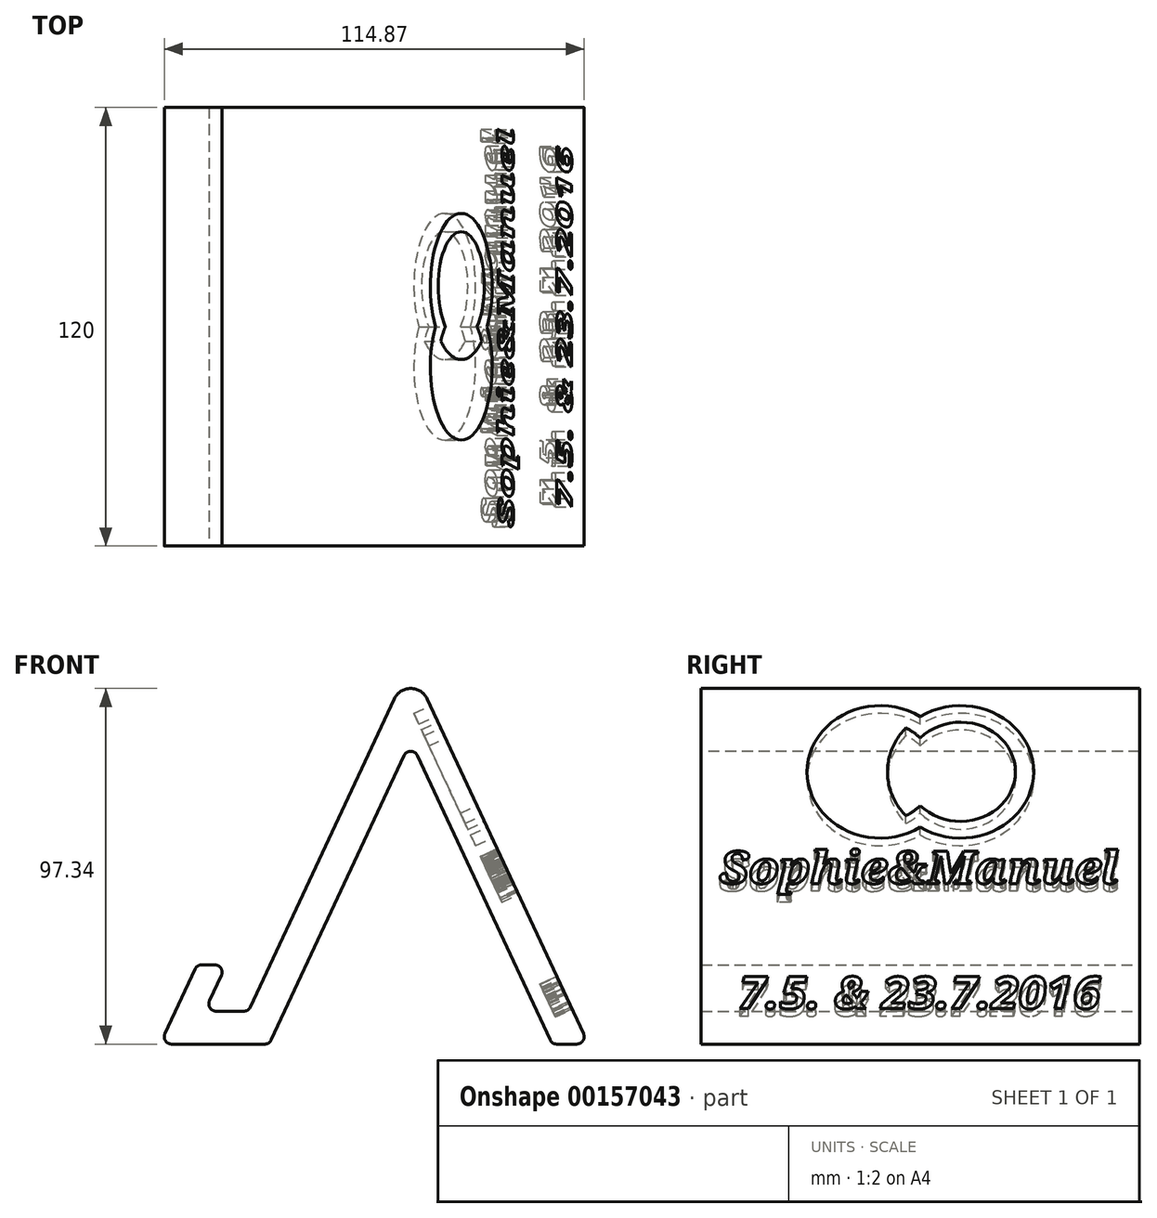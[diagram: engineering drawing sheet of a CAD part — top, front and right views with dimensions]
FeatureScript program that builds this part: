
annotation { "Feature Type Name" : "Feature", "Feature Type Description" : "" }
export const myFeature = defineFeature(function(context is Context, id is Id, definition is map)
    precondition{}
    {
        {
            var Q0;
            Q0=qCreatedBy(makeId("Front.planeOp"),FACE);
            var sketch = newSketch(context, id + "F0", { "sketchPlane" : qUnion([Q0])});
            skLineSegment(sketch, "E0", {"start": v(-35.91, 1.37) * mm, "end": v(-27.91, 1.37) * mm});
            skLineSegment(sketch, "E1", {"start": v(-27.91, 1.37) * mm, "end": v(-33.83, -11.32) * mm});
            skLineSegment(sketch, "E2", {"start": v(-33.83, -11.32) * mm, "end": v(-21.83, -11.32) * mm});
            skLineSegment(sketch, "E3", {"start": v(-21.83, -11.32) * mm, "end": v(22.55, 83.85) * mm});
            skLineSegment(sketch, "E4", {"start": v(22.55, 83.85) * mm, "end": v(22.55, 83.85) * mm});
            skLineSegment(sketch, "E5", {"start": v(22.55, 83.85) * mm, "end": v(71.12, -20.32) * mm});
            skLineSegment(sketch, "E6", {"start": v(71.12, -20.32) * mm, "end": v(61.19, -20.32) * mm});
            skLineSegment(sketch, "E7", {"start": v(61.19, -20.32) * mm, "end": v(22.55, 62.55) * mm});
            skLineSegment(sketch, "E8", {"start": v(22.55, 62.55) * mm, "end": v(-16.1, -20.32) * mm});
            skLineSegment(sketch, "E9", {"start": v(-46.03, -20.32) * mm, "end": v(-35.91, 1.37) * mm});
            skLineSegment(sketch, "E10", {"start": v(-16.1, -20.32) * mm, "end": v(61.19, -20.32) * mm, "construction": true});
            skLineSegment(sketch, "E11", {"start": v(-46.03, -20.32) * mm, "end": v(-16.1, -20.32) * mm});
            skSolve(sketch);
        }
        {
            var Q0;
            Q0=makeQuery(id+"F0.imprint","IMPRINT",FACE,{"disambiguationData":[TD([[makeQuery(id+"F0.imprint","IMPRINT",EDGE,{"derivedFrom":sQuery(id+"F0.wireOp",EDGE,"E0")}),-1.0]])]});
            extrude(context, id + "F1", {"entities" : qUnion([Q0]), "depth" : 120 * mm});
        }
        {
            var Q0;
            Q0=makeQuery(id+"F1.opExtrude","SWEPT_FACE",FACE,{"disambiguationData":[OSD([sQuery(id+"F0.wireOp",EDGE,"E5")])]});
            var sketch = newSketch(context, id + "F2", { "sketchPlane" : qUnion([Q0])});
            skText(sketch, "E12", { "text": "Sophie&Manuel", "fontName": "NotoSerif-BoldItalic.ttf"});
            skLineSegment(sketch, "E13", {"start": v(-120, 23.74) * mm, "end": v(0, 23.74) * mm, "construction": true});
            skLineSegment(sketch, "E14", {"start": v(-60, 23.74) * mm, "end": v(-60, 33.74) * mm, "construction": true});
            skLineSegment(sketch, "E15", {"start": v(-60, 33.74) * mm, "end": v(-71, 33.74) * mm, "construction": true});
            skLineSegment(sketch, "E16", {"start": v(-60, 33.74) * mm, "end": v(-49, 33.74) * mm, "construction": true});
            skCircle(sketch, "E17", {"center": v(-71, 33.74) * mm, "radius": 20 * mm});
            skCircle(sketch, "E18", {"center": v(-71, 33.74) * mm, "radius": 15 * mm});
            skCircle(sketch, "E19", {"center": v(-49, 33.74) * mm, "radius": 15 * mm});
            skCircle(sketch, "E20", {"center": v(-49, 33.74) * mm, "radius": 20 * mm});
            skLineSegment(sketch, "E21", {"start": v(-60, 0) * mm, "end": v(-60, -48.47) * mm, "construction": true});
            skText(sketch, "E22", { "text": "7.5. & 23.7.2016", "fontName": "OpenSans-BoldItalic.ttf"});
            const initialGuessF2  = {"E12": [-0.115, 0, 1, 0, 0.00981], "E22": [-0.10981, -0.03778, 1, 0, 0.00973]};
            skSetInitialGuess(sketch, initialGuessF2);
            skSolve(sketch);
        }
        {
            var Q0;
            Q0=makeQuery(id+"F2.imprint","IMPRINT",FACE,{"disambiguationData":[TD([[makeQuery(id+"F2.imprint","IMPRINT",EDGE,{"derivedFrom":sQuery(id+"F2.wireOp",EDGE,"E12.sketch_text.stroke-154")}),-1.0]])]});
            var Q1;
            Q1=makeQuery(id+"F2.imprint","IMPRINT",FACE,{"disambiguationData":[TD([[makeQuery(id+"F2.imprint","IMPRINT",EDGE,{"derivedFrom":sQuery(id+"F2.wireOp",EDGE,"E12.sketch_text.stroke-88")}),-1.0]])]});
            var Q2;
            Q2=makeQuery(id+"F2.imprint","IMPRINT",FACE,{"disambiguationData":[TD([[makeQuery(id+"F2.imprint","IMPRINT",EDGE,{"derivedFrom":sQuery(id+"F2.wireOp",EDGE,"E12.sketch_text.stroke-52")}),-1.0]])]});
            var Q3;
            Q3 = qSketchRegion(id + "F2", true);
            var Q4;
            {var subQ0=sQuery(id+"F2.wireOp",EDGE,"E19");var subQ1=sQuery(id+"F2.wireOp",EDGE,"E17");var subQ2=makeQuery(id+"F2.imprint","INTERSECT",VERTEX,{"disambiguationData":[OD(0.0)],"derivedFrom":[subQ1,subQ0]});Q4=makeQuery(id+"F2.imprint","IMPRINT",FACE,{"disambiguationData":[TD([[makeQuery(id+"F2.imprint","IMPRINT",EDGE,{"disambiguationData":[TD([[subQ2,1.0]])],"derivedFrom":subQ1}),1.0]])]});}
            var Q5;
            {var subQ0=sQuery(id+"F2.wireOp",EDGE,"E20");var subQ1=sQuery(id+"F2.wireOp",EDGE,"E18");var subQ2=makeQuery(id+"F2.imprint","INTERSECT",VERTEX,{"disambiguationData":[OD(0.0)],"derivedFrom":[subQ1,subQ0]});Q5=makeQuery(id+"F2.imprint","IMPRINT",FACE,{"disambiguationData":[TD([[makeQuery(id+"F2.imprint","IMPRINT",EDGE,{"disambiguationData":[TD([[subQ2,1.0]])],"derivedFrom":subQ1}),1.0]])]});}
            extrude(context, id + "F3", {"entities" : qUnion([Q0, Q1, Q2, Q3, Q4, Q5]), "operationType" : NewBodyOperationType.REMOVE, "oppositeDirection" : true, "depth" : 5 * mm});
        }
        {
            var Q0;
            Q0=makeQuery(id+"F1.opExtrude","SWEPT_EDGE",EDGE,{"disambiguationData":[OSD([sQuery(id+"F0.wireOp",EDGE,"E3"),sQuery(id+"F0.wireOp",EDGE,"E5")])]});
            fillet(context, id + "F4", {"entities" : qUnion([Q0]), "radius" : 5 * mm, "tangentPropagation" : true, "allowEdgeOverflow" : false});
        }
        {
            var Q0;
            Q0=makeQuery(id+"F1.opExtrude","SWEPT_EDGE",EDGE,{"disambiguationData":[OSD([sQuery(id+"F0.wireOp",EDGE,"E0"),sQuery(id+"F0.wireOp",EDGE,"E1")])]});
            var Q1;
            Q1=makeQuery(id+"F1.opExtrude","SWEPT_EDGE",EDGE,{"disambiguationData":[OSD([sQuery(id+"F0.wireOp",EDGE,"E0"),sQuery(id+"F0.wireOp",EDGE,"E9")])]});
            var Q2;
            Q2=makeQuery(id+"F1.opExtrude","SWEPT_EDGE",EDGE,{"disambiguationData":[OSD([sQuery(id+"F0.wireOp",EDGE,"E1"),sQuery(id+"F0.wireOp",EDGE,"E2")])]});
            var Q3;
            Q3=makeQuery(id+"F1.opExtrude","SWEPT_EDGE",EDGE,{"disambiguationData":[OSD([sQuery(id+"F0.wireOp",EDGE,"E2"),sQuery(id+"F0.wireOp",EDGE,"E3")])]});
            var Q4;
            Q4=makeQuery(id+"F1.opExtrude","SWEPT_EDGE",EDGE,{"disambiguationData":[OSD([sQuery(id+"F0.wireOp",EDGE,"E9"),sQuery(id+"F0.wireOp",EDGE,"E11")])]});
            var Q5;
            Q5=makeQuery(id+"F1.opExtrude","SWEPT_EDGE",EDGE,{"disambiguationData":[OSD([sQuery(id+"F0.wireOp",EDGE,"E8"),sQuery(id+"F0.wireOp",EDGE,"E11")])]});
            var Q6;
            Q6=makeQuery(id+"F1.opExtrude","SWEPT_EDGE",EDGE,{"disambiguationData":[OSD([sQuery(id+"F0.wireOp",EDGE,"E6"),sQuery(id+"F0.wireOp",EDGE,"E7")])]});
            var Q7;
            Q7=makeQuery(id+"F1.opExtrude","SWEPT_EDGE",EDGE,{"disambiguationData":[OSD([sQuery(id+"F0.wireOp",EDGE,"E5"),sQuery(id+"F0.wireOp",EDGE,"E6")])]});
            fillet(context, id + "F5", {"entities" : qUnion([Q0, Q1, Q2, Q3, Q4, Q5, Q6, Q7]), "radius" : 2 * mm, "tangentPropagation" : true, "allowEdgeOverflow" : false});
        }
        {
            var Q0;
            Q0=makeQuery(id+"F1.opExtrude","SWEPT_EDGE",EDGE,{"disambiguationData":[OSD([sQuery(id+"F0.wireOp",EDGE,"E7"),sQuery(id+"F0.wireOp",EDGE,"E8")])]});
            fillet(context, id + "F6", {"entities" : qUnion([Q0]), "radius" : 2 * mm, "tangentPropagation" : true, "allowEdgeOverflow" : false});
        }
        {
            var Q0;
            Q0=makeQuery(id+"F3.boolean.opBoolean","COPY",FACE,{"derivedFrom":makeQuery(id+"F3.opExtrude","CAP_FACE",FACE,{"disambiguationData":[OSD([sQuery(id+"F2.wireOp",EDGE,"E12.sketch_text.stroke-52"),sQuery(id+"F2.wireOp",EDGE,"E12.sketch_text.stroke-53"),sQuery(id+"F2.wireOp",EDGE,"E12.sketch_text.stroke-54"),sQuery(id+"F2.wireOp",EDGE,"E12.sketch_text.stroke-55"),sQuery(id+"F2.wireOp",EDGE,"E12.sketch_text.stroke-56"),sQuery(id+"F2.wireOp",EDGE,"E12.sketch_text.stroke-57"),sQuery(id+"F2.wireOp",EDGE,"E12.sketch_text.stroke-58"),sQuery(id+"F2.wireOp",EDGE,"E12.sketch_text.stroke-59"),sQuery(id+"F2.wireOp",EDGE,"E12.sketch_text.stroke-60"),sQuery(id+"F2.wireOp",EDGE,"E12.sketch_text.stroke-61"),sQuery(id+"F2.wireOp",EDGE,"E12.sketch_text.stroke-62"),sQuery(id+"F2.wireOp",EDGE,"E12.sketch_text.stroke-63"),sQuery(id+"F2.wireOp",EDGE,"E12.sketch_text.stroke-64"),sQuery(id+"F2.wireOp",EDGE,"E12.sketch_text.stroke-65"),sQuery(id+"F2.wireOp",EDGE,"E12.sketch_text.stroke-66"),sQuery(id+"F2.wireOp",EDGE,"E12.sketch_text.stroke-67"),sQuery(id+"F2.wireOp",EDGE,"E12.sketch_text.stroke-68"),sQuery(id+"F2.wireOp",EDGE,"E12.sketch_text.stroke-69"),sQuery(id+"F2.wireOp",EDGE,"E12.sketch_text.stroke-70"),sQuery(id+"F2.wireOp",EDGE,"E12.sketch_text.stroke-71"),sQuery(id+"F2.wireOp",EDGE,"E12.sketch_text.stroke-72"),sQuery(id+"F2.wireOp",EDGE,"E12.sketch_text.stroke-73"),sQuery(id+"F2.wireOp",EDGE,"E12.sketch_text.stroke-74"),sQuery(id+"F2.wireOp",EDGE,"E12.sketch_text.stroke-75"),sQuery(id+"F2.wireOp",EDGE,"E12.sketch_text.stroke-76"),sQuery(id+"F2.wireOp",EDGE,"E12.sketch_text.stroke-77"),sQuery(id+"F2.wireOp",EDGE,"E12.sketch_text.stroke-78"),sQuery(id+"F2.wireOp",EDGE,"E12.sketch_text.stroke-79"),sQuery(id+"F2.wireOp",EDGE,"E12.sketch_text.stroke-80"),sQuery(id+"F2.wireOp",EDGE,"E12.sketch_text.stroke-81"),sQuery(id+"F2.wireOp",EDGE,"E12.sketch_text.stroke-82"),sQuery(id+"F2.wireOp",EDGE,"E12.sketch_text.stroke-83"),sQuery(id+"F2.wireOp",EDGE,"E12.sketch_text.stroke-84"),sQuery(id+"F2.wireOp",EDGE,"E12.sketch_text.stroke-85"),sQuery(id+"F2.wireOp",EDGE,"E12.sketch_text.stroke-86"),sQuery(id+"F2.wireOp",EDGE,"E12.sketch_text.stroke-87")])],"isStart":false})});
            var Q1;
            Q1=makeQuery(id+"F3.boolean.opBoolean","COPY",FACE,{"derivedFrom":makeQuery(id+"F3.opExtrude","CAP_FACE",FACE,{"disambiguationData":[OSD([sQuery(id+"F2.wireOp",EDGE,"E12.sketch_text.stroke-0"),sQuery(id+"F2.wireOp",EDGE,"E12.sketch_text.stroke-1"),sQuery(id+"F2.wireOp",EDGE,"E12.sketch_text.stroke-2"),sQuery(id+"F2.wireOp",EDGE,"E12.sketch_text.stroke-3"),sQuery(id+"F2.wireOp",EDGE,"E12.sketch_text.stroke-4"),sQuery(id+"F2.wireOp",EDGE,"E12.sketch_text.stroke-5"),sQuery(id+"F2.wireOp",EDGE,"E12.sketch_text.stroke-6"),sQuery(id+"F2.wireOp",EDGE,"E12.sketch_text.stroke-7"),sQuery(id+"F2.wireOp",EDGE,"E12.sketch_text.stroke-8"),sQuery(id+"F2.wireOp",EDGE,"E12.sketch_text.stroke-9"),sQuery(id+"F2.wireOp",EDGE,"E12.sketch_text.stroke-10"),sQuery(id+"F2.wireOp",EDGE,"E12.sketch_text.stroke-11"),sQuery(id+"F2.wireOp",EDGE,"E12.sketch_text.stroke-12"),sQuery(id+"F2.wireOp",EDGE,"E12.sketch_text.stroke-13"),sQuery(id+"F2.wireOp",EDGE,"E12.sketch_text.stroke-14"),sQuery(id+"F2.wireOp",EDGE,"E12.sketch_text.stroke-15"),sQuery(id+"F2.wireOp",EDGE,"E12.sketch_text.stroke-16"),sQuery(id+"F2.wireOp",EDGE,"E12.sketch_text.stroke-17"),sQuery(id+"F2.wireOp",EDGE,"E12.sketch_text.stroke-18"),sQuery(id+"F2.wireOp",EDGE,"E12.sketch_text.stroke-19"),sQuery(id+"F2.wireOp",EDGE,"E12.sketch_text.stroke-20"),sQuery(id+"F2.wireOp",EDGE,"E12.sketch_text.stroke-21"),sQuery(id+"F2.wireOp",EDGE,"E12.sketch_text.stroke-22"),sQuery(id+"F2.wireOp",EDGE,"E12.sketch_text.stroke-23"),sQuery(id+"F2.wireOp",EDGE,"E12.sketch_text.stroke-24"),sQuery(id+"F2.wireOp",EDGE,"E12.sketch_text.stroke-25"),sQuery(id+"F2.wireOp",EDGE,"E12.sketch_text.stroke-26"),sQuery(id+"F2.wireOp",EDGE,"E12.sketch_text.stroke-27"),sQuery(id+"F2.wireOp",EDGE,"E12.sketch_text.stroke-28"),sQuery(id+"F2.wireOp",EDGE,"E12.sketch_text.stroke-29"),sQuery(id+"F2.wireOp",EDGE,"E12.sketch_text.stroke-30"),sQuery(id+"F2.wireOp",EDGE,"E12.sketch_text.stroke-31"),sQuery(id+"F2.wireOp",EDGE,"E12.sketch_text.stroke-32"),sQuery(id+"F2.wireOp",EDGE,"E12.sketch_text.stroke-33"),sQuery(id+"F2.wireOp",EDGE,"E12.sketch_text.stroke-34"),sQuery(id+"F2.wireOp",EDGE,"E12.sketch_text.stroke-35"),sQuery(id+"F2.wireOp",EDGE,"E12.sketch_text.stroke-36"),sQuery(id+"F2.wireOp",EDGE,"E12.sketch_text.stroke-37"),sQuery(id+"F2.wireOp",EDGE,"E12.sketch_text.stroke-38"),sQuery(id+"F2.wireOp",EDGE,"E12.sketch_text.stroke-39"),sQuery(id+"F2.wireOp",EDGE,"E12.sketch_text.stroke-40"),sQuery(id+"F2.wireOp",EDGE,"E12.sketch_text.stroke-41"),sQuery(id+"F2.wireOp",EDGE,"E12.sketch_text.stroke-42"),sQuery(id+"F2.wireOp",EDGE,"E12.sketch_text.stroke-43"),sQuery(id+"F2.wireOp",EDGE,"E12.sketch_text.stroke-44"),sQuery(id+"F2.wireOp",EDGE,"E12.sketch_text.stroke-45"),sQuery(id+"F2.wireOp",EDGE,"E12.sketch_text.stroke-46"),sQuery(id+"F2.wireOp",EDGE,"E12.sketch_text.stroke-47"),sQuery(id+"F2.wireOp",EDGE,"E12.sketch_text.stroke-48"),sQuery(id+"F2.wireOp",EDGE,"E12.sketch_text.stroke-49"),sQuery(id+"F2.wireOp",EDGE,"E12.sketch_text.stroke-50"),sQuery(id+"F2.wireOp",EDGE,"E12.sketch_text.stroke-51")])],"isStart":false})});
            var Q2;
            Q2=makeQuery(id+"F3.boolean.opBoolean","COPY",FACE,{"derivedFrom":makeQuery(id+"F3.opExtrude","CAP_FACE",FACE,{"disambiguationData":[OSD([sQuery(id+"F2.wireOp",EDGE,"E12.sketch_text.stroke-88"),sQuery(id+"F2.wireOp",EDGE,"E12.sketch_text.stroke-89"),sQuery(id+"F2.wireOp",EDGE,"E12.sketch_text.stroke-90"),sQuery(id+"F2.wireOp",EDGE,"E12.sketch_text.stroke-91"),sQuery(id+"F2.wireOp",EDGE,"E12.sketch_text.stroke-92"),sQuery(id+"F2.wireOp",EDGE,"E12.sketch_text.stroke-93"),sQuery(id+"F2.wireOp",EDGE,"E12.sketch_text.stroke-94"),sQuery(id+"F2.wireOp",EDGE,"E12.sketch_text.stroke-95"),sQuery(id+"F2.wireOp",EDGE,"E12.sketch_text.stroke-96"),sQuery(id+"F2.wireOp",EDGE,"E12.sketch_text.stroke-97"),sQuery(id+"F2.wireOp",EDGE,"E12.sketch_text.stroke-98"),sQuery(id+"F2.wireOp",EDGE,"E12.sketch_text.stroke-99"),sQuery(id+"F2.wireOp",EDGE,"E12.sketch_text.stroke-100"),sQuery(id+"F2.wireOp",EDGE,"E12.sketch_text.stroke-101"),sQuery(id+"F2.wireOp",EDGE,"E12.sketch_text.stroke-102"),sQuery(id+"F2.wireOp",EDGE,"E12.sketch_text.stroke-103"),sQuery(id+"F2.wireOp",EDGE,"E12.sketch_text.stroke-104"),sQuery(id+"F2.wireOp",EDGE,"E12.sketch_text.stroke-105"),sQuery(id+"F2.wireOp",EDGE,"E12.sketch_text.stroke-106"),sQuery(id+"F2.wireOp",EDGE,"E12.sketch_text.stroke-107"),sQuery(id+"F2.wireOp",EDGE,"E12.sketch_text.stroke-108"),sQuery(id+"F2.wireOp",EDGE,"E12.sketch_text.stroke-109"),sQuery(id+"F2.wireOp",EDGE,"E12.sketch_text.stroke-110"),sQuery(id+"F2.wireOp",EDGE,"E12.sketch_text.stroke-111"),sQuery(id+"F2.wireOp",EDGE,"E12.sketch_text.stroke-112"),sQuery(id+"F2.wireOp",EDGE,"E12.sketch_text.stroke-113"),sQuery(id+"F2.wireOp",EDGE,"E12.sketch_text.stroke-114"),sQuery(id+"F2.wireOp",EDGE,"E12.sketch_text.stroke-115"),sQuery(id+"F2.wireOp",EDGE,"E12.sketch_text.stroke-116"),sQuery(id+"F2.wireOp",EDGE,"E12.sketch_text.stroke-117"),sQuery(id+"F2.wireOp",EDGE,"E12.sketch_text.stroke-118"),sQuery(id+"F2.wireOp",EDGE,"E12.sketch_text.stroke-119"),sQuery(id+"F2.wireOp",EDGE,"E12.sketch_text.stroke-120"),sQuery(id+"F2.wireOp",EDGE,"E12.sketch_text.stroke-121"),sQuery(id+"F2.wireOp",EDGE,"E12.sketch_text.stroke-122"),sQuery(id+"F2.wireOp",EDGE,"E12.sketch_text.stroke-123"),sQuery(id+"F2.wireOp",EDGE,"E12.sketch_text.stroke-124"),sQuery(id+"F2.wireOp",EDGE,"E12.sketch_text.stroke-125"),sQuery(id+"F2.wireOp",EDGE,"E12.sketch_text.stroke-126"),sQuery(id+"F2.wireOp",EDGE,"E12.sketch_text.stroke-127"),sQuery(id+"F2.wireOp",EDGE,"E12.sketch_text.stroke-128"),sQuery(id+"F2.wireOp",EDGE,"E12.sketch_text.stroke-129"),sQuery(id+"F2.wireOp",EDGE,"E12.sketch_text.stroke-130"),sQuery(id+"F2.wireOp",EDGE,"E12.sketch_text.stroke-131"),sQuery(id+"F2.wireOp",EDGE,"E12.sketch_text.stroke-132"),sQuery(id+"F2.wireOp",EDGE,"E12.sketch_text.stroke-133"),sQuery(id+"F2.wireOp",EDGE,"E12.sketch_text.stroke-134"),sQuery(id+"F2.wireOp",EDGE,"E12.sketch_text.stroke-135"),sQuery(id+"F2.wireOp",EDGE,"E12.sketch_text.stroke-136"),sQuery(id+"F2.wireOp",EDGE,"E12.sketch_text.stroke-137"),sQuery(id+"F2.wireOp",EDGE,"E12.sketch_text.stroke-138"),sQuery(id+"F2.wireOp",EDGE,"E12.sketch_text.stroke-139"),sQuery(id+"F2.wireOp",EDGE,"E12.sketch_text.stroke-140"),sQuery(id+"F2.wireOp",EDGE,"E12.sketch_text.stroke-141"),sQuery(id+"F2.wireOp",EDGE,"E12.sketch_text.stroke-142"),sQuery(id+"F2.wireOp",EDGE,"E12.sketch_text.stroke-143"),sQuery(id+"F2.wireOp",EDGE,"E12.sketch_text.stroke-144"),sQuery(id+"F2.wireOp",EDGE,"E12.sketch_text.stroke-145"),sQuery(id+"F2.wireOp",EDGE,"E12.sketch_text.stroke-146"),sQuery(id+"F2.wireOp",EDGE,"E12.sketch_text.stroke-147"),sQuery(id+"F2.wireOp",EDGE,"E12.sketch_text.stroke-148"),sQuery(id+"F2.wireOp",EDGE,"E12.sketch_text.stroke-149"),sQuery(id+"F2.wireOp",EDGE,"E12.sketch_text.stroke-150"),sQuery(id+"F2.wireOp",EDGE,"E12.sketch_text.stroke-151"),sQuery(id+"F2.wireOp",EDGE,"E12.sketch_text.stroke-152"),sQuery(id+"F2.wireOp",EDGE,"E12.sketch_text.stroke-153")])],"isStart":false})});
            var Q3;
            Q3=makeQuery(id+"F3.boolean.opBoolean","COPY",FACE,{"derivedFrom":makeQuery(id+"F3.opExtrude","CAP_FACE",FACE,{"disambiguationData":[OSD([sQuery(id+"F2.wireOp",EDGE,"E12.sketch_text.stroke-154"),sQuery(id+"F2.wireOp",EDGE,"E12.sketch_text.stroke-155"),sQuery(id+"F2.wireOp",EDGE,"E12.sketch_text.stroke-156"),sQuery(id+"F2.wireOp",EDGE,"E12.sketch_text.stroke-157"),sQuery(id+"F2.wireOp",EDGE,"E12.sketch_text.stroke-158"),sQuery(id+"F2.wireOp",EDGE,"E12.sketch_text.stroke-159"),sQuery(id+"F2.wireOp",EDGE,"E12.sketch_text.stroke-160"),sQuery(id+"F2.wireOp",EDGE,"E12.sketch_text.stroke-161"),sQuery(id+"F2.wireOp",EDGE,"E12.sketch_text.stroke-162"),sQuery(id+"F2.wireOp",EDGE,"E12.sketch_text.stroke-163"),sQuery(id+"F2.wireOp",EDGE,"E12.sketch_text.stroke-164"),sQuery(id+"F2.wireOp",EDGE,"E12.sketch_text.stroke-165"),sQuery(id+"F2.wireOp",EDGE,"E12.sketch_text.stroke-166"),sQuery(id+"F2.wireOp",EDGE,"E12.sketch_text.stroke-167"),sQuery(id+"F2.wireOp",EDGE,"E12.sketch_text.stroke-168"),sQuery(id+"F2.wireOp",EDGE,"E12.sketch_text.stroke-169"),sQuery(id+"F2.wireOp",EDGE,"E12.sketch_text.stroke-170"),sQuery(id+"F2.wireOp",EDGE,"E12.sketch_text.stroke-171"),sQuery(id+"F2.wireOp",EDGE,"E12.sketch_text.stroke-172"),sQuery(id+"F2.wireOp",EDGE,"E12.sketch_text.stroke-173"),sQuery(id+"F2.wireOp",EDGE,"E12.sketch_text.stroke-174"),sQuery(id+"F2.wireOp",EDGE,"E12.sketch_text.stroke-175"),sQuery(id+"F2.wireOp",EDGE,"E12.sketch_text.stroke-176"),sQuery(id+"F2.wireOp",EDGE,"E12.sketch_text.stroke-177"),sQuery(id+"F2.wireOp",EDGE,"E12.sketch_text.stroke-178"),sQuery(id+"F2.wireOp",EDGE,"E12.sketch_text.stroke-179"),sQuery(id+"F2.wireOp",EDGE,"E12.sketch_text.stroke-180"),sQuery(id+"F2.wireOp",EDGE,"E12.sketch_text.stroke-181"),sQuery(id+"F2.wireOp",EDGE,"E12.sketch_text.stroke-182"),sQuery(id+"F2.wireOp",EDGE,"E12.sketch_text.stroke-183"),sQuery(id+"F2.wireOp",EDGE,"E12.sketch_text.stroke-184"),sQuery(id+"F2.wireOp",EDGE,"E12.sketch_text.stroke-185"),sQuery(id+"F2.wireOp",EDGE,"E12.sketch_text.stroke-186"),sQuery(id+"F2.wireOp",EDGE,"E12.sketch_text.stroke-187"),sQuery(id+"F2.wireOp",EDGE,"E12.sketch_text.stroke-188"),sQuery(id+"F2.wireOp",EDGE,"E12.sketch_text.stroke-189"),sQuery(id+"F2.wireOp",EDGE,"E12.sketch_text.stroke-190"),sQuery(id+"F2.wireOp",EDGE,"E12.sketch_text.stroke-191"),sQuery(id+"F2.wireOp",EDGE,"E12.sketch_text.stroke-192"),sQuery(id+"F2.wireOp",EDGE,"E12.sketch_text.stroke-193"),sQuery(id+"F2.wireOp",EDGE,"E12.sketch_text.stroke-194"),sQuery(id+"F2.wireOp",EDGE,"E12.sketch_text.stroke-195"),sQuery(id+"F2.wireOp",EDGE,"E12.sketch_text.stroke-196"),sQuery(id+"F2.wireOp",EDGE,"E12.sketch_text.stroke-197"),sQuery(id+"F2.wireOp",EDGE,"E12.sketch_text.stroke-198"),sQuery(id+"F2.wireOp",EDGE,"E12.sketch_text.stroke-199"),sQuery(id+"F2.wireOp",EDGE,"E12.sketch_text.stroke-200"),sQuery(id+"F2.wireOp",EDGE,"E12.sketch_text.stroke-201"),sQuery(id+"F2.wireOp",EDGE,"E12.sketch_text.stroke-202"),sQuery(id+"F2.wireOp",EDGE,"E12.sketch_text.stroke-203"),sQuery(id+"F2.wireOp",EDGE,"E12.sketch_text.stroke-204"),sQuery(id+"F2.wireOp",EDGE,"E12.sketch_text.stroke-205"),sQuery(id+"F2.wireOp",EDGE,"E12.sketch_text.stroke-206"),sQuery(id+"F2.wireOp",EDGE,"E12.sketch_text.stroke-207"),sQuery(id+"F2.wireOp",EDGE,"E12.sketch_text.stroke-208"),sQuery(id+"F2.wireOp",EDGE,"E12.sketch_text.stroke-209"),sQuery(id+"F2.wireOp",EDGE,"E12.sketch_text.stroke-210"),sQuery(id+"F2.wireOp",EDGE,"E12.sketch_text.stroke-211"),sQuery(id+"F2.wireOp",EDGE,"E12.sketch_text.stroke-212"),sQuery(id+"F2.wireOp",EDGE,"E12.sketch_text.stroke-213"),sQuery(id+"F2.wireOp",EDGE,"E12.sketch_text.stroke-214"),sQuery(id+"F2.wireOp",EDGE,"E12.sketch_text.stroke-215")])],"isStart":false})});
            var Q4;
            Q4=makeQuery(id+"F3.boolean.opBoolean","COPY",FACE,{"derivedFrom":makeQuery(id+"F3.opExtrude","CAP_FACE",FACE,{"disambiguationData":[OSD([sQuery(id+"F2.wireOp",EDGE,"E12.sketch_text.stroke-216"),sQuery(id+"F2.wireOp",EDGE,"E12.sketch_text.stroke-217"),sQuery(id+"F2.wireOp",EDGE,"E12.sketch_text.stroke-218"),sQuery(id+"F2.wireOp",EDGE,"E12.sketch_text.stroke-219"),sQuery(id+"F2.wireOp",EDGE,"E12.sketch_text.stroke-220"),sQuery(id+"F2.wireOp",EDGE,"E12.sketch_text.stroke-221"),sQuery(id+"F2.wireOp",EDGE,"E12.sketch_text.stroke-222"),sQuery(id+"F2.wireOp",EDGE,"E12.sketch_text.stroke-223"),sQuery(id+"F2.wireOp",EDGE,"E12.sketch_text.stroke-224"),sQuery(id+"F2.wireOp",EDGE,"E12.sketch_text.stroke-225"),sQuery(id+"F2.wireOp",EDGE,"E12.sketch_text.stroke-226"),sQuery(id+"F2.wireOp",EDGE,"E12.sketch_text.stroke-227"),sQuery(id+"F2.wireOp",EDGE,"E12.sketch_text.stroke-228"),sQuery(id+"F2.wireOp",EDGE,"E12.sketch_text.stroke-229"),sQuery(id+"F2.wireOp",EDGE,"E12.sketch_text.stroke-230"),sQuery(id+"F2.wireOp",EDGE,"E12.sketch_text.stroke-231"),sQuery(id+"F2.wireOp",EDGE,"E12.sketch_text.stroke-232"),sQuery(id+"F2.wireOp",EDGE,"E12.sketch_text.stroke-233"),sQuery(id+"F2.wireOp",EDGE,"E12.sketch_text.stroke-234"),sQuery(id+"F2.wireOp",EDGE,"E12.sketch_text.stroke-235"),sQuery(id+"F2.wireOp",EDGE,"E12.sketch_text.stroke-236"),sQuery(id+"F2.wireOp",EDGE,"E12.sketch_text.stroke-237"),sQuery(id+"F2.wireOp",EDGE,"E12.sketch_text.stroke-238"),sQuery(id+"F2.wireOp",EDGE,"E12.sketch_text.stroke-239"),sQuery(id+"F2.wireOp",EDGE,"E12.sketch_text.stroke-240"),sQuery(id+"F2.wireOp",EDGE,"E12.sketch_text.stroke-241"),sQuery(id+"F2.wireOp",EDGE,"E12.sketch_text.stroke-242"),sQuery(id+"F2.wireOp",EDGE,"E12.sketch_text.stroke-243")])],"isStart":false})});
            var Q5;
            Q5=makeQuery(id+"F3.boolean.opBoolean","COPY",FACE,{"derivedFrom":makeQuery(id+"F3.opExtrude","CAP_FACE",FACE,{"disambiguationData":[OSD([sQuery(id+"F2.wireOp",EDGE,"E12.sketch_text.stroke-260"),sQuery(id+"F2.wireOp",EDGE,"E12.sketch_text.stroke-261"),sQuery(id+"F2.wireOp",EDGE,"E12.sketch_text.stroke-262"),sQuery(id+"F2.wireOp",EDGE,"E12.sketch_text.stroke-263"),sQuery(id+"F2.wireOp",EDGE,"E12.sketch_text.stroke-264"),sQuery(id+"F2.wireOp",EDGE,"E12.sketch_text.stroke-265"),sQuery(id+"F2.wireOp",EDGE,"E12.sketch_text.stroke-266"),sQuery(id+"F2.wireOp",EDGE,"E12.sketch_text.stroke-267"),sQuery(id+"F2.wireOp",EDGE,"E12.sketch_text.stroke-268"),sQuery(id+"F2.wireOp",EDGE,"E12.sketch_text.stroke-269"),sQuery(id+"F2.wireOp",EDGE,"E12.sketch_text.stroke-270"),sQuery(id+"F2.wireOp",EDGE,"E12.sketch_text.stroke-271"),sQuery(id+"F2.wireOp",EDGE,"E12.sketch_text.stroke-272"),sQuery(id+"F2.wireOp",EDGE,"E12.sketch_text.stroke-273"),sQuery(id+"F2.wireOp",EDGE,"E12.sketch_text.stroke-274"),sQuery(id+"F2.wireOp",EDGE,"E12.sketch_text.stroke-275"),sQuery(id+"F2.wireOp",EDGE,"E12.sketch_text.stroke-276"),sQuery(id+"F2.wireOp",EDGE,"E12.sketch_text.stroke-277"),sQuery(id+"F2.wireOp",EDGE,"E12.sketch_text.stroke-278"),sQuery(id+"F2.wireOp",EDGE,"E12.sketch_text.stroke-279"),sQuery(id+"F2.wireOp",EDGE,"E12.sketch_text.stroke-280"),sQuery(id+"F2.wireOp",EDGE,"E12.sketch_text.stroke-281"),sQuery(id+"F2.wireOp",EDGE,"E12.sketch_text.stroke-282"),sQuery(id+"F2.wireOp",EDGE,"E12.sketch_text.stroke-283"),sQuery(id+"F2.wireOp",EDGE,"E12.sketch_text.stroke-284"),sQuery(id+"F2.wireOp",EDGE,"E12.sketch_text.stroke-285"),sQuery(id+"F2.wireOp",EDGE,"E12.sketch_text.stroke-286"),sQuery(id+"F2.wireOp",EDGE,"E12.sketch_text.stroke-287"),sQuery(id+"F2.wireOp",EDGE,"E12.sketch_text.stroke-288"),sQuery(id+"F2.wireOp",EDGE,"E12.sketch_text.stroke-289"),sQuery(id+"F2.wireOp",EDGE,"E12.sketch_text.stroke-290"),sQuery(id+"F2.wireOp",EDGE,"E12.sketch_text.stroke-291"),sQuery(id+"F2.wireOp",EDGE,"E12.sketch_text.stroke-292"),sQuery(id+"F2.wireOp",EDGE,"E12.sketch_text.stroke-293"),sQuery(id+"F2.wireOp",EDGE,"E12.sketch_text.stroke-294"),sQuery(id+"F2.wireOp",EDGE,"E12.sketch_text.stroke-295"),sQuery(id+"F2.wireOp",EDGE,"E12.sketch_text.stroke-296"),sQuery(id+"F2.wireOp",EDGE,"E12.sketch_text.stroke-297"),sQuery(id+"F2.wireOp",EDGE,"E12.sketch_text.stroke-298"),sQuery(id+"F2.wireOp",EDGE,"E12.sketch_text.stroke-299"),sQuery(id+"F2.wireOp",EDGE,"E12.sketch_text.stroke-300"),sQuery(id+"F2.wireOp",EDGE,"E12.sketch_text.stroke-301"),sQuery(id+"F2.wireOp",EDGE,"E12.sketch_text.stroke-302")])],"isStart":false})});
            var Q6;
            Q6=makeQuery(id+"F3.boolean.opBoolean","COPY",FACE,{"derivedFrom":makeQuery(id+"F3.opExtrude","CAP_FACE",FACE,{"disambiguationData":[OSD([sQuery(id+"F2.wireOp",EDGE,"E12.sketch_text.stroke-303"),sQuery(id+"F2.wireOp",EDGE,"E12.sketch_text.stroke-304"),sQuery(id+"F2.wireOp",EDGE,"E12.sketch_text.stroke-305"),sQuery(id+"F2.wireOp",EDGE,"E12.sketch_text.stroke-306"),sQuery(id+"F2.wireOp",EDGE,"E12.sketch_text.stroke-307"),sQuery(id+"F2.wireOp",EDGE,"E12.sketch_text.stroke-308"),sQuery(id+"F2.wireOp",EDGE,"E12.sketch_text.stroke-309"),sQuery(id+"F2.wireOp",EDGE,"E12.sketch_text.stroke-310"),sQuery(id+"F2.wireOp",EDGE,"E12.sketch_text.stroke-311"),sQuery(id+"F2.wireOp",EDGE,"E12.sketch_text.stroke-312"),sQuery(id+"F2.wireOp",EDGE,"E12.sketch_text.stroke-313"),sQuery(id+"F2.wireOp",EDGE,"E12.sketch_text.stroke-314"),sQuery(id+"F2.wireOp",EDGE,"E12.sketch_text.stroke-315"),sQuery(id+"F2.wireOp",EDGE,"E12.sketch_text.stroke-316"),sQuery(id+"F2.wireOp",EDGE,"E12.sketch_text.stroke-317"),sQuery(id+"F2.wireOp",EDGE,"E12.sketch_text.stroke-318"),sQuery(id+"F2.wireOp",EDGE,"E12.sketch_text.stroke-319"),sQuery(id+"F2.wireOp",EDGE,"E12.sketch_text.stroke-320"),sQuery(id+"F2.wireOp",EDGE,"E12.sketch_text.stroke-321"),sQuery(id+"F2.wireOp",EDGE,"E12.sketch_text.stroke-322"),sQuery(id+"F2.wireOp",EDGE,"E12.sketch_text.stroke-323"),sQuery(id+"F2.wireOp",EDGE,"E12.sketch_text.stroke-324"),sQuery(id+"F2.wireOp",EDGE,"E12.sketch_text.stroke-325"),sQuery(id+"F2.wireOp",EDGE,"E12.sketch_text.stroke-326"),sQuery(id+"F2.wireOp",EDGE,"E12.sketch_text.stroke-327"),sQuery(id+"F2.wireOp",EDGE,"E12.sketch_text.stroke-328"),sQuery(id+"F2.wireOp",EDGE,"E12.sketch_text.stroke-329"),sQuery(id+"F2.wireOp",EDGE,"E12.sketch_text.stroke-330"),sQuery(id+"F2.wireOp",EDGE,"E12.sketch_text.stroke-331"),sQuery(id+"F2.wireOp",EDGE,"E12.sketch_text.stroke-332"),sQuery(id+"F2.wireOp",EDGE,"E12.sketch_text.stroke-333"),sQuery(id+"F2.wireOp",EDGE,"E12.sketch_text.stroke-334"),sQuery(id+"F2.wireOp",EDGE,"E12.sketch_text.stroke-335"),sQuery(id+"F2.wireOp",EDGE,"E12.sketch_text.stroke-336"),sQuery(id+"F2.wireOp",EDGE,"E12.sketch_text.stroke-337"),sQuery(id+"F2.wireOp",EDGE,"E12.sketch_text.stroke-338"),sQuery(id+"F2.wireOp",EDGE,"E12.sketch_text.stroke-339"),sQuery(id+"F2.wireOp",EDGE,"E12.sketch_text.stroke-340"),sQuery(id+"F2.wireOp",EDGE,"E12.sketch_text.stroke-341"),sQuery(id+"F2.wireOp",EDGE,"E12.sketch_text.stroke-342"),sQuery(id+"F2.wireOp",EDGE,"E12.sketch_text.stroke-343"),sQuery(id+"F2.wireOp",EDGE,"E12.sketch_text.stroke-344"),sQuery(id+"F2.wireOp",EDGE,"E12.sketch_text.stroke-345"),sQuery(id+"F2.wireOp",EDGE,"E12.sketch_text.stroke-346"),sQuery(id+"F2.wireOp",EDGE,"E12.sketch_text.stroke-347"),sQuery(id+"F2.wireOp",EDGE,"E12.sketch_text.stroke-348"),sQuery(id+"F2.wireOp",EDGE,"E12.sketch_text.stroke-349"),sQuery(id+"F2.wireOp",EDGE,"E12.sketch_text.stroke-350"),sQuery(id+"F2.wireOp",EDGE,"E12.sketch_text.stroke-351"),sQuery(id+"F2.wireOp",EDGE,"E12.sketch_text.stroke-352"),sQuery(id+"F2.wireOp",EDGE,"E12.sketch_text.stroke-353"),sQuery(id+"F2.wireOp",EDGE,"E12.sketch_text.stroke-354"),sQuery(id+"F2.wireOp",EDGE,"E12.sketch_text.stroke-355"),sQuery(id+"F2.wireOp",EDGE,"E12.sketch_text.stroke-356"),sQuery(id+"F2.wireOp",EDGE,"E12.sketch_text.stroke-357"),sQuery(id+"F2.wireOp",EDGE,"E12.sketch_text.stroke-358"),sQuery(id+"F2.wireOp",EDGE,"E12.sketch_text.stroke-359"),sQuery(id+"F2.wireOp",EDGE,"E12.sketch_text.stroke-360"),sQuery(id+"F2.wireOp",EDGE,"E12.sketch_text.stroke-361"),sQuery(id+"F2.wireOp",EDGE,"E12.sketch_text.stroke-362"),sQuery(id+"F2.wireOp",EDGE,"E12.sketch_text.stroke-363"),sQuery(id+"F2.wireOp",EDGE,"E12.sketch_text.stroke-364"),sQuery(id+"F2.wireOp",EDGE,"E12.sketch_text.stroke-365"),sQuery(id+"F2.wireOp",EDGE,"E12.sketch_text.stroke-366"),sQuery(id+"F2.wireOp",EDGE,"E12.sketch_text.stroke-367"),sQuery(id+"F2.wireOp",EDGE,"E12.sketch_text.stroke-368"),sQuery(id+"F2.wireOp",EDGE,"E12.sketch_text.stroke-369")])],"isStart":false})});
            var Q7;
            Q7=makeQuery(id+"F3.boolean.opBoolean","COPY",FACE,{"derivedFrom":makeQuery(id+"F3.opExtrude","CAP_FACE",FACE,{"disambiguationData":[OSD([sQuery(id+"F2.wireOp",EDGE,"E12.sketch_text.stroke-370"),sQuery(id+"F2.wireOp",EDGE,"E12.sketch_text.stroke-371"),sQuery(id+"F2.wireOp",EDGE,"E12.sketch_text.stroke-372"),sQuery(id+"F2.wireOp",EDGE,"E12.sketch_text.stroke-373"),sQuery(id+"F2.wireOp",EDGE,"E12.sketch_text.stroke-374"),sQuery(id+"F2.wireOp",EDGE,"E12.sketch_text.stroke-375"),sQuery(id+"F2.wireOp",EDGE,"E12.sketch_text.stroke-376"),sQuery(id+"F2.wireOp",EDGE,"E12.sketch_text.stroke-377"),sQuery(id+"F2.wireOp",EDGE,"E12.sketch_text.stroke-378"),sQuery(id+"F2.wireOp",EDGE,"E12.sketch_text.stroke-379"),sQuery(id+"F2.wireOp",EDGE,"E12.sketch_text.stroke-380"),sQuery(id+"F2.wireOp",EDGE,"E12.sketch_text.stroke-381"),sQuery(id+"F2.wireOp",EDGE,"E12.sketch_text.stroke-382"),sQuery(id+"F2.wireOp",EDGE,"E12.sketch_text.stroke-383"),sQuery(id+"F2.wireOp",EDGE,"E12.sketch_text.stroke-384"),sQuery(id+"F2.wireOp",EDGE,"E12.sketch_text.stroke-385"),sQuery(id+"F2.wireOp",EDGE,"E12.sketch_text.stroke-386"),sQuery(id+"F2.wireOp",EDGE,"E12.sketch_text.stroke-387"),sQuery(id+"F2.wireOp",EDGE,"E12.sketch_text.stroke-388"),sQuery(id+"F2.wireOp",EDGE,"E12.sketch_text.stroke-389"),sQuery(id+"F2.wireOp",EDGE,"E12.sketch_text.stroke-390"),sQuery(id+"F2.wireOp",EDGE,"E12.sketch_text.stroke-391"),sQuery(id+"F2.wireOp",EDGE,"E12.sketch_text.stroke-392"),sQuery(id+"F2.wireOp",EDGE,"E12.sketch_text.stroke-393"),sQuery(id+"F2.wireOp",EDGE,"E12.sketch_text.stroke-394"),sQuery(id+"F2.wireOp",EDGE,"E12.sketch_text.stroke-395"),sQuery(id+"F2.wireOp",EDGE,"E12.sketch_text.stroke-396"),sQuery(id+"F2.wireOp",EDGE,"E12.sketch_text.stroke-397"),sQuery(id+"F2.wireOp",EDGE,"E12.sketch_text.stroke-398"),sQuery(id+"F2.wireOp",EDGE,"E12.sketch_text.stroke-399"),sQuery(id+"F2.wireOp",EDGE,"E12.sketch_text.stroke-400"),sQuery(id+"F2.wireOp",EDGE,"E12.sketch_text.stroke-401"),sQuery(id+"F2.wireOp",EDGE,"E12.sketch_text.stroke-402"),sQuery(id+"F2.wireOp",EDGE,"E12.sketch_text.stroke-403"),sQuery(id+"F2.wireOp",EDGE,"E12.sketch_text.stroke-404"),sQuery(id+"F2.wireOp",EDGE,"E12.sketch_text.stroke-405"),sQuery(id+"F2.wireOp",EDGE,"E12.sketch_text.stroke-406"),sQuery(id+"F2.wireOp",EDGE,"E12.sketch_text.stroke-407"),sQuery(id+"F2.wireOp",EDGE,"E12.sketch_text.stroke-408"),sQuery(id+"F2.wireOp",EDGE,"E12.sketch_text.stroke-409"),sQuery(id+"F2.wireOp",EDGE,"E12.sketch_text.stroke-410"),sQuery(id+"F2.wireOp",EDGE,"E12.sketch_text.stroke-411"),sQuery(id+"F2.wireOp",EDGE,"E12.sketch_text.stroke-412"),sQuery(id+"F2.wireOp",EDGE,"E12.sketch_text.stroke-413"),sQuery(id+"F2.wireOp",EDGE,"E12.sketch_text.stroke-414"),sQuery(id+"F2.wireOp",EDGE,"E12.sketch_text.stroke-415"),sQuery(id+"F2.wireOp",EDGE,"E12.sketch_text.stroke-416"),sQuery(id+"F2.wireOp",EDGE,"E12.sketch_text.stroke-417"),sQuery(id+"F2.wireOp",EDGE,"E12.sketch_text.stroke-418"),sQuery(id+"F2.wireOp",EDGE,"E12.sketch_text.stroke-419"),sQuery(id+"F2.wireOp",EDGE,"E12.sketch_text.stroke-420"),sQuery(id+"F2.wireOp",EDGE,"E12.sketch_text.stroke-421"),sQuery(id+"F2.wireOp",EDGE,"E12.sketch_text.stroke-422"),sQuery(id+"F2.wireOp",EDGE,"E12.sketch_text.stroke-423")])],"isStart":false})});
            var Q8;
            Q8=makeQuery(id+"F3.boolean.opBoolean","COPY",FACE,{"derivedFrom":makeQuery(id+"F3.opExtrude","CAP_FACE",FACE,{"disambiguationData":[OSD([sQuery(id+"F2.wireOp",EDGE,"E12.sketch_text.stroke-424"),sQuery(id+"F2.wireOp",EDGE,"E12.sketch_text.stroke-425"),sQuery(id+"F2.wireOp",EDGE,"E12.sketch_text.stroke-426"),sQuery(id+"F2.wireOp",EDGE,"E12.sketch_text.stroke-427"),sQuery(id+"F2.wireOp",EDGE,"E12.sketch_text.stroke-428"),sQuery(id+"F2.wireOp",EDGE,"E12.sketch_text.stroke-429"),sQuery(id+"F2.wireOp",EDGE,"E12.sketch_text.stroke-430"),sQuery(id+"F2.wireOp",EDGE,"E12.sketch_text.stroke-431"),sQuery(id+"F2.wireOp",EDGE,"E12.sketch_text.stroke-432"),sQuery(id+"F2.wireOp",EDGE,"E12.sketch_text.stroke-433"),sQuery(id+"F2.wireOp",EDGE,"E12.sketch_text.stroke-434"),sQuery(id+"F2.wireOp",EDGE,"E12.sketch_text.stroke-435"),sQuery(id+"F2.wireOp",EDGE,"E12.sketch_text.stroke-436"),sQuery(id+"F2.wireOp",EDGE,"E12.sketch_text.stroke-437"),sQuery(id+"F2.wireOp",EDGE,"E12.sketch_text.stroke-438"),sQuery(id+"F2.wireOp",EDGE,"E12.sketch_text.stroke-439"),sQuery(id+"F2.wireOp",EDGE,"E12.sketch_text.stroke-440"),sQuery(id+"F2.wireOp",EDGE,"E12.sketch_text.stroke-441"),sQuery(id+"F2.wireOp",EDGE,"E12.sketch_text.stroke-442"),sQuery(id+"F2.wireOp",EDGE,"E12.sketch_text.stroke-443"),sQuery(id+"F2.wireOp",EDGE,"E12.sketch_text.stroke-444"),sQuery(id+"F2.wireOp",EDGE,"E12.sketch_text.stroke-445"),sQuery(id+"F2.wireOp",EDGE,"E12.sketch_text.stroke-446"),sQuery(id+"F2.wireOp",EDGE,"E12.sketch_text.stroke-447"),sQuery(id+"F2.wireOp",EDGE,"E12.sketch_text.stroke-448"),sQuery(id+"F2.wireOp",EDGE,"E12.sketch_text.stroke-449"),sQuery(id+"F2.wireOp",EDGE,"E12.sketch_text.stroke-450"),sQuery(id+"F2.wireOp",EDGE,"E12.sketch_text.stroke-451"),sQuery(id+"F2.wireOp",EDGE,"E12.sketch_text.stroke-452"),sQuery(id+"F2.wireOp",EDGE,"E12.sketch_text.stroke-453"),sQuery(id+"F2.wireOp",EDGE,"E12.sketch_text.stroke-454"),sQuery(id+"F2.wireOp",EDGE,"E12.sketch_text.stroke-455"),sQuery(id+"F2.wireOp",EDGE,"E12.sketch_text.stroke-456"),sQuery(id+"F2.wireOp",EDGE,"E12.sketch_text.stroke-457"),sQuery(id+"F2.wireOp",EDGE,"E12.sketch_text.stroke-458"),sQuery(id+"F2.wireOp",EDGE,"E12.sketch_text.stroke-459"),sQuery(id+"F2.wireOp",EDGE,"E12.sketch_text.stroke-460"),sQuery(id+"F2.wireOp",EDGE,"E12.sketch_text.stroke-461"),sQuery(id+"F2.wireOp",EDGE,"E12.sketch_text.stroke-462"),sQuery(id+"F2.wireOp",EDGE,"E12.sketch_text.stroke-463"),sQuery(id+"F2.wireOp",EDGE,"E12.sketch_text.stroke-464"),sQuery(id+"F2.wireOp",EDGE,"E12.sketch_text.stroke-465"),sQuery(id+"F2.wireOp",EDGE,"E12.sketch_text.stroke-466"),sQuery(id+"F2.wireOp",EDGE,"E12.sketch_text.stroke-467"),sQuery(id+"F2.wireOp",EDGE,"E12.sketch_text.stroke-468"),sQuery(id+"F2.wireOp",EDGE,"E12.sketch_text.stroke-469"),sQuery(id+"F2.wireOp",EDGE,"E12.sketch_text.stroke-470"),sQuery(id+"F2.wireOp",EDGE,"E12.sketch_text.stroke-471"),sQuery(id+"F2.wireOp",EDGE,"E12.sketch_text.stroke-472"),sQuery(id+"F2.wireOp",EDGE,"E12.sketch_text.stroke-473"),sQuery(id+"F2.wireOp",EDGE,"E12.sketch_text.stroke-474"),sQuery(id+"F2.wireOp",EDGE,"E12.sketch_text.stroke-475"),sQuery(id+"F2.wireOp",EDGE,"E12.sketch_text.stroke-476"),sQuery(id+"F2.wireOp",EDGE,"E12.sketch_text.stroke-477"),sQuery(id+"F2.wireOp",EDGE,"E12.sketch_text.stroke-478"),sQuery(id+"F2.wireOp",EDGE,"E12.sketch_text.stroke-479")])],"isStart":false})});
            var Q9;
            Q9=makeQuery(id+"F3.boolean.opBoolean","COPY",FACE,{"derivedFrom":makeQuery(id+"F3.opExtrude","CAP_FACE",FACE,{"disambiguationData":[OSD([sQuery(id+"F2.wireOp",EDGE,"E12.sketch_text.stroke-480"),sQuery(id+"F2.wireOp",EDGE,"E12.sketch_text.stroke-481"),sQuery(id+"F2.wireOp",EDGE,"E12.sketch_text.stroke-482"),sQuery(id+"F2.wireOp",EDGE,"E12.sketch_text.stroke-483"),sQuery(id+"F2.wireOp",EDGE,"E12.sketch_text.stroke-484"),sQuery(id+"F2.wireOp",EDGE,"E12.sketch_text.stroke-485"),sQuery(id+"F2.wireOp",EDGE,"E12.sketch_text.stroke-486"),sQuery(id+"F2.wireOp",EDGE,"E12.sketch_text.stroke-487"),sQuery(id+"F2.wireOp",EDGE,"E12.sketch_text.stroke-488"),sQuery(id+"F2.wireOp",EDGE,"E12.sketch_text.stroke-489"),sQuery(id+"F2.wireOp",EDGE,"E12.sketch_text.stroke-490"),sQuery(id+"F2.wireOp",EDGE,"E12.sketch_text.stroke-491"),sQuery(id+"F2.wireOp",EDGE,"E12.sketch_text.stroke-492"),sQuery(id+"F2.wireOp",EDGE,"E12.sketch_text.stroke-493"),sQuery(id+"F2.wireOp",EDGE,"E12.sketch_text.stroke-494"),sQuery(id+"F2.wireOp",EDGE,"E12.sketch_text.stroke-495"),sQuery(id+"F2.wireOp",EDGE,"E12.sketch_text.stroke-496"),sQuery(id+"F2.wireOp",EDGE,"E12.sketch_text.stroke-497"),sQuery(id+"F2.wireOp",EDGE,"E12.sketch_text.stroke-498"),sQuery(id+"F2.wireOp",EDGE,"E12.sketch_text.stroke-499"),sQuery(id+"F2.wireOp",EDGE,"E12.sketch_text.stroke-500"),sQuery(id+"F2.wireOp",EDGE,"E12.sketch_text.stroke-501"),sQuery(id+"F2.wireOp",EDGE,"E12.sketch_text.stroke-502"),sQuery(id+"F2.wireOp",EDGE,"E12.sketch_text.stroke-503"),sQuery(id+"F2.wireOp",EDGE,"E12.sketch_text.stroke-504"),sQuery(id+"F2.wireOp",EDGE,"E12.sketch_text.stroke-505"),sQuery(id+"F2.wireOp",EDGE,"E12.sketch_text.stroke-506"),sQuery(id+"F2.wireOp",EDGE,"E12.sketch_text.stroke-507"),sQuery(id+"F2.wireOp",EDGE,"E12.sketch_text.stroke-508"),sQuery(id+"F2.wireOp",EDGE,"E12.sketch_text.stroke-509"),sQuery(id+"F2.wireOp",EDGE,"E12.sketch_text.stroke-510"),sQuery(id+"F2.wireOp",EDGE,"E12.sketch_text.stroke-511"),sQuery(id+"F2.wireOp",EDGE,"E12.sketch_text.stroke-512"),sQuery(id+"F2.wireOp",EDGE,"E12.sketch_text.stroke-513"),sQuery(id+"F2.wireOp",EDGE,"E12.sketch_text.stroke-514"),sQuery(id+"F2.wireOp",EDGE,"E12.sketch_text.stroke-515"),sQuery(id+"F2.wireOp",EDGE,"E12.sketch_text.stroke-516"),sQuery(id+"F2.wireOp",EDGE,"E12.sketch_text.stroke-517"),sQuery(id+"F2.wireOp",EDGE,"E12.sketch_text.stroke-518"),sQuery(id+"F2.wireOp",EDGE,"E12.sketch_text.stroke-519"),sQuery(id+"F2.wireOp",EDGE,"E12.sketch_text.stroke-520"),sQuery(id+"F2.wireOp",EDGE,"E12.sketch_text.stroke-521"),sQuery(id+"F2.wireOp",EDGE,"E12.sketch_text.stroke-522"),sQuery(id+"F2.wireOp",EDGE,"E12.sketch_text.stroke-523"),sQuery(id+"F2.wireOp",EDGE,"E12.sketch_text.stroke-524"),sQuery(id+"F2.wireOp",EDGE,"E12.sketch_text.stroke-525"),sQuery(id+"F2.wireOp",EDGE,"E12.sketch_text.stroke-526"),sQuery(id+"F2.wireOp",EDGE,"E12.sketch_text.stroke-527"),sQuery(id+"F2.wireOp",EDGE,"E12.sketch_text.stroke-528"),sQuery(id+"F2.wireOp",EDGE,"E12.sketch_text.stroke-529"),sQuery(id+"F2.wireOp",EDGE,"E12.sketch_text.stroke-530"),sQuery(id+"F2.wireOp",EDGE,"E12.sketch_text.stroke-531"),sQuery(id+"F2.wireOp",EDGE,"E12.sketch_text.stroke-532"),sQuery(id+"F2.wireOp",EDGE,"E12.sketch_text.stroke-533"),sQuery(id+"F2.wireOp",EDGE,"E12.sketch_text.stroke-534"),sQuery(id+"F2.wireOp",EDGE,"E12.sketch_text.stroke-535"),sQuery(id+"F2.wireOp",EDGE,"E12.sketch_text.stroke-536"),sQuery(id+"F2.wireOp",EDGE,"E12.sketch_text.stroke-537")])],"isStart":false})});
            var Q10;
            Q10=makeQuery(id+"F3.boolean.opBoolean","COPY",FACE,{"derivedFrom":makeQuery(id+"F3.opExtrude","CAP_FACE",FACE,{"disambiguationData":[OSD([sQuery(id+"F2.wireOp",EDGE,"E12.sketch_text.stroke-480"),sQuery(id+"F2.wireOp",EDGE,"E12.sketch_text.stroke-481"),sQuery(id+"F2.wireOp",EDGE,"E12.sketch_text.stroke-482"),sQuery(id+"F2.wireOp",EDGE,"E12.sketch_text.stroke-483"),sQuery(id+"F2.wireOp",EDGE,"E12.sketch_text.stroke-484"),sQuery(id+"F2.wireOp",EDGE,"E12.sketch_text.stroke-485"),sQuery(id+"F2.wireOp",EDGE,"E12.sketch_text.stroke-486"),sQuery(id+"F2.wireOp",EDGE,"E12.sketch_text.stroke-487"),sQuery(id+"F2.wireOp",EDGE,"E12.sketch_text.stroke-488"),sQuery(id+"F2.wireOp",EDGE,"E12.sketch_text.stroke-489"),sQuery(id+"F2.wireOp",EDGE,"E12.sketch_text.stroke-490"),sQuery(id+"F2.wireOp",EDGE,"E12.sketch_text.stroke-491"),sQuery(id+"F2.wireOp",EDGE,"E12.sketch_text.stroke-492"),sQuery(id+"F2.wireOp",EDGE,"E12.sketch_text.stroke-493"),sQuery(id+"F2.wireOp",EDGE,"E12.sketch_text.stroke-494"),sQuery(id+"F2.wireOp",EDGE,"E12.sketch_text.stroke-495"),sQuery(id+"F2.wireOp",EDGE,"E12.sketch_text.stroke-496"),sQuery(id+"F2.wireOp",EDGE,"E12.sketch_text.stroke-497"),sQuery(id+"F2.wireOp",EDGE,"E12.sketch_text.stroke-498"),sQuery(id+"F2.wireOp",EDGE,"E12.sketch_text.stroke-499"),sQuery(id+"F2.wireOp",EDGE,"E12.sketch_text.stroke-500"),sQuery(id+"F2.wireOp",EDGE,"E12.sketch_text.stroke-501"),sQuery(id+"F2.wireOp",EDGE,"E12.sketch_text.stroke-502"),sQuery(id+"F2.wireOp",EDGE,"E12.sketch_text.stroke-503"),sQuery(id+"F2.wireOp",EDGE,"E12.sketch_text.stroke-504"),sQuery(id+"F2.wireOp",EDGE,"E12.sketch_text.stroke-505"),sQuery(id+"F2.wireOp",EDGE,"E12.sketch_text.stroke-506"),sQuery(id+"F2.wireOp",EDGE,"E12.sketch_text.stroke-507"),sQuery(id+"F2.wireOp",EDGE,"E12.sketch_text.stroke-508"),sQuery(id+"F2.wireOp",EDGE,"E12.sketch_text.stroke-509"),sQuery(id+"F2.wireOp",EDGE,"E12.sketch_text.stroke-510"),sQuery(id+"F2.wireOp",EDGE,"E12.sketch_text.stroke-511"),sQuery(id+"F2.wireOp",EDGE,"E12.sketch_text.stroke-512"),sQuery(id+"F2.wireOp",EDGE,"E12.sketch_text.stroke-513"),sQuery(id+"F2.wireOp",EDGE,"E12.sketch_text.stroke-514"),sQuery(id+"F2.wireOp",EDGE,"E12.sketch_text.stroke-515"),sQuery(id+"F2.wireOp",EDGE,"E12.sketch_text.stroke-516"),sQuery(id+"F2.wireOp",EDGE,"E12.sketch_text.stroke-517"),sQuery(id+"F2.wireOp",EDGE,"E12.sketch_text.stroke-518"),sQuery(id+"F2.wireOp",EDGE,"E12.sketch_text.stroke-519"),sQuery(id+"F2.wireOp",EDGE,"E12.sketch_text.stroke-520"),sQuery(id+"F2.wireOp",EDGE,"E12.sketch_text.stroke-521"),sQuery(id+"F2.wireOp",EDGE,"E12.sketch_text.stroke-522"),sQuery(id+"F2.wireOp",EDGE,"E12.sketch_text.stroke-523"),sQuery(id+"F2.wireOp",EDGE,"E12.sketch_text.stroke-524"),sQuery(id+"F2.wireOp",EDGE,"E12.sketch_text.stroke-525"),sQuery(id+"F2.wireOp",EDGE,"E12.sketch_text.stroke-526"),sQuery(id+"F2.wireOp",EDGE,"E12.sketch_text.stroke-527"),sQuery(id+"F2.wireOp",EDGE,"E12.sketch_text.stroke-528"),sQuery(id+"F2.wireOp",EDGE,"E12.sketch_text.stroke-529"),sQuery(id+"F2.wireOp",EDGE,"E12.sketch_text.stroke-530"),sQuery(id+"F2.wireOp",EDGE,"E12.sketch_text.stroke-531"),sQuery(id+"F2.wireOp",EDGE,"E12.sketch_text.stroke-532"),sQuery(id+"F2.wireOp",EDGE,"E12.sketch_text.stroke-533"),sQuery(id+"F2.wireOp",EDGE,"E12.sketch_text.stroke-534"),sQuery(id+"F2.wireOp",EDGE,"E12.sketch_text.stroke-535"),sQuery(id+"F2.wireOp",EDGE,"E12.sketch_text.stroke-536"),sQuery(id+"F2.wireOp",EDGE,"E12.sketch_text.stroke-537")])],"isStart":false})});
            var Q11;
            Q11=makeQuery(id+"F3.boolean.opBoolean","COPY",FACE,{"derivedFrom":makeQuery(id+"F3.opExtrude","CAP_FACE",FACE,{"disambiguationData":[OSD([sQuery(id+"F2.wireOp",EDGE,"E12.sketch_text.stroke-538"),sQuery(id+"F2.wireOp",EDGE,"E12.sketch_text.stroke-539"),sQuery(id+"F2.wireOp",EDGE,"E12.sketch_text.stroke-540"),sQuery(id+"F2.wireOp",EDGE,"E12.sketch_text.stroke-541"),sQuery(id+"F2.wireOp",EDGE,"E12.sketch_text.stroke-542"),sQuery(id+"F2.wireOp",EDGE,"E12.sketch_text.stroke-543"),sQuery(id+"F2.wireOp",EDGE,"E12.sketch_text.stroke-544"),sQuery(id+"F2.wireOp",EDGE,"E12.sketch_text.stroke-545"),sQuery(id+"F2.wireOp",EDGE,"E12.sketch_text.stroke-546"),sQuery(id+"F2.wireOp",EDGE,"E12.sketch_text.stroke-547"),sQuery(id+"F2.wireOp",EDGE,"E12.sketch_text.stroke-548"),sQuery(id+"F2.wireOp",EDGE,"E12.sketch_text.stroke-549"),sQuery(id+"F2.wireOp",EDGE,"E12.sketch_text.stroke-550"),sQuery(id+"F2.wireOp",EDGE,"E12.sketch_text.stroke-551"),sQuery(id+"F2.wireOp",EDGE,"E12.sketch_text.stroke-552"),sQuery(id+"F2.wireOp",EDGE,"E12.sketch_text.stroke-553"),sQuery(id+"F2.wireOp",EDGE,"E12.sketch_text.stroke-554"),sQuery(id+"F2.wireOp",EDGE,"E12.sketch_text.stroke-555"),sQuery(id+"F2.wireOp",EDGE,"E12.sketch_text.stroke-556"),sQuery(id+"F2.wireOp",EDGE,"E12.sketch_text.stroke-557"),sQuery(id+"F2.wireOp",EDGE,"E12.sketch_text.stroke-558"),sQuery(id+"F2.wireOp",EDGE,"E12.sketch_text.stroke-559"),sQuery(id+"F2.wireOp",EDGE,"E12.sketch_text.stroke-560"),sQuery(id+"F2.wireOp",EDGE,"E12.sketch_text.stroke-561"),sQuery(id+"F2.wireOp",EDGE,"E12.sketch_text.stroke-562"),sQuery(id+"F2.wireOp",EDGE,"E12.sketch_text.stroke-563"),sQuery(id+"F2.wireOp",EDGE,"E12.sketch_text.stroke-564"),sQuery(id+"F2.wireOp",EDGE,"E12.sketch_text.stroke-565"),sQuery(id+"F2.wireOp",EDGE,"E12.sketch_text.stroke-566"),sQuery(id+"F2.wireOp",EDGE,"E12.sketch_text.stroke-567"),sQuery(id+"F2.wireOp",EDGE,"E12.sketch_text.stroke-568"),sQuery(id+"F2.wireOp",EDGE,"E12.sketch_text.stroke-569"),sQuery(id+"F2.wireOp",EDGE,"E12.sketch_text.stroke-570"),sQuery(id+"F2.wireOp",EDGE,"E12.sketch_text.stroke-571"),sQuery(id+"F2.wireOp",EDGE,"E12.sketch_text.stroke-572"),sQuery(id+"F2.wireOp",EDGE,"E12.sketch_text.stroke-573"),sQuery(id+"F2.wireOp",EDGE,"E12.sketch_text.stroke-574"),sQuery(id+"F2.wireOp",EDGE,"E12.sketch_text.stroke-575"),sQuery(id+"F2.wireOp",EDGE,"E12.sketch_text.stroke-576"),sQuery(id+"F2.wireOp",EDGE,"E12.sketch_text.stroke-577"),sQuery(id+"F2.wireOp",EDGE,"E12.sketch_text.stroke-578"),sQuery(id+"F2.wireOp",EDGE,"E12.sketch_text.stroke-579"),sQuery(id+"F2.wireOp",EDGE,"E12.sketch_text.stroke-580"),sQuery(id+"F2.wireOp",EDGE,"E12.sketch_text.stroke-581"),sQuery(id+"F2.wireOp",EDGE,"E12.sketch_text.stroke-582"),sQuery(id+"F2.wireOp",EDGE,"E12.sketch_text.stroke-583"),sQuery(id+"F2.wireOp",EDGE,"E12.sketch_text.stroke-584"),sQuery(id+"F2.wireOp",EDGE,"E12.sketch_text.stroke-585"),sQuery(id+"F2.wireOp",EDGE,"E12.sketch_text.stroke-586"),sQuery(id+"F2.wireOp",EDGE,"E12.sketch_text.stroke-587"),sQuery(id+"F2.wireOp",EDGE,"E12.sketch_text.stroke-588"),sQuery(id+"F2.wireOp",EDGE,"E12.sketch_text.stroke-589")])],"isStart":false})});
            var Q12;
            Q12=makeQuery(id+"F3.boolean.opBoolean","COPY",FACE,{"derivedFrom":makeQuery(id+"F3.opExtrude","CAP_FACE",FACE,{"disambiguationData":[OSD([sQuery(id+"F2.wireOp",EDGE,"E12.sketch_text.stroke-590"),sQuery(id+"F2.wireOp",EDGE,"E12.sketch_text.stroke-591"),sQuery(id+"F2.wireOp",EDGE,"E12.sketch_text.stroke-592"),sQuery(id+"F2.wireOp",EDGE,"E12.sketch_text.stroke-593"),sQuery(id+"F2.wireOp",EDGE,"E12.sketch_text.stroke-594"),sQuery(id+"F2.wireOp",EDGE,"E12.sketch_text.stroke-595"),sQuery(id+"F2.wireOp",EDGE,"E12.sketch_text.stroke-596"),sQuery(id+"F2.wireOp",EDGE,"E12.sketch_text.stroke-597"),sQuery(id+"F2.wireOp",EDGE,"E12.sketch_text.stroke-598"),sQuery(id+"F2.wireOp",EDGE,"E12.sketch_text.stroke-599"),sQuery(id+"F2.wireOp",EDGE,"E12.sketch_text.stroke-600"),sQuery(id+"F2.wireOp",EDGE,"E12.sketch_text.stroke-601"),sQuery(id+"F2.wireOp",EDGE,"E12.sketch_text.stroke-602"),sQuery(id+"F2.wireOp",EDGE,"E12.sketch_text.stroke-603"),sQuery(id+"F2.wireOp",EDGE,"E12.sketch_text.stroke-604"),sQuery(id+"F2.wireOp",EDGE,"E12.sketch_text.stroke-605"),sQuery(id+"F2.wireOp",EDGE,"E12.sketch_text.stroke-606"),sQuery(id+"F2.wireOp",EDGE,"E12.sketch_text.stroke-607"),sQuery(id+"F2.wireOp",EDGE,"E12.sketch_text.stroke-608"),sQuery(id+"F2.wireOp",EDGE,"E12.sketch_text.stroke-609"),sQuery(id+"F2.wireOp",EDGE,"E12.sketch_text.stroke-610"),sQuery(id+"F2.wireOp",EDGE,"E12.sketch_text.stroke-611"),sQuery(id+"F2.wireOp",EDGE,"E12.sketch_text.stroke-612"),sQuery(id+"F2.wireOp",EDGE,"E12.sketch_text.stroke-613"),sQuery(id+"F2.wireOp",EDGE,"E12.sketch_text.stroke-614"),sQuery(id+"F2.wireOp",EDGE,"E12.sketch_text.stroke-615"),sQuery(id+"F2.wireOp",EDGE,"E12.sketch_text.stroke-616"),sQuery(id+"F2.wireOp",EDGE,"E12.sketch_text.stroke-617"),sQuery(id+"F2.wireOp",EDGE,"E12.sketch_text.stroke-618"),sQuery(id+"F2.wireOp",EDGE,"E12.sketch_text.stroke-619"),sQuery(id+"F2.wireOp",EDGE,"E12.sketch_text.stroke-620"),sQuery(id+"F2.wireOp",EDGE,"E12.sketch_text.stroke-621"),sQuery(id+"F2.wireOp",EDGE,"E12.sketch_text.stroke-622"),sQuery(id+"F2.wireOp",EDGE,"E12.sketch_text.stroke-623"),sQuery(id+"F2.wireOp",EDGE,"E12.sketch_text.stroke-624"),sQuery(id+"F2.wireOp",EDGE,"E12.sketch_text.stroke-625"),sQuery(id+"F2.wireOp",EDGE,"E12.sketch_text.stroke-626"),sQuery(id+"F2.wireOp",EDGE,"E12.sketch_text.stroke-627"),sQuery(id+"F2.wireOp",EDGE,"E12.sketch_text.stroke-628"),sQuery(id+"F2.wireOp",EDGE,"E12.sketch_text.stroke-629"),sQuery(id+"F2.wireOp",EDGE,"E12.sketch_text.stroke-630"),sQuery(id+"F2.wireOp",EDGE,"E12.sketch_text.stroke-631"),sQuery(id+"F2.wireOp",EDGE,"E12.sketch_text.stroke-632")])],"isStart":false})});
            var Q13;
            Q13=makeQuery(id+"F3.boolean.opBoolean","COPY",FACE,{"derivedFrom":makeQuery(id+"F3.opExtrude","CAP_FACE",FACE,{"disambiguationData":[OSD([sQuery(id+"F2.wireOp",EDGE,"E12.sketch_text.stroke-633"),sQuery(id+"F2.wireOp",EDGE,"E12.sketch_text.stroke-634"),sQuery(id+"F2.wireOp",EDGE,"E12.sketch_text.stroke-635"),sQuery(id+"F2.wireOp",EDGE,"E12.sketch_text.stroke-636"),sQuery(id+"F2.wireOp",EDGE,"E12.sketch_text.stroke-637"),sQuery(id+"F2.wireOp",EDGE,"E12.sketch_text.stroke-638"),sQuery(id+"F2.wireOp",EDGE,"E12.sketch_text.stroke-639"),sQuery(id+"F2.wireOp",EDGE,"E12.sketch_text.stroke-640"),sQuery(id+"F2.wireOp",EDGE,"E12.sketch_text.stroke-641"),sQuery(id+"F2.wireOp",EDGE,"E12.sketch_text.stroke-642"),sQuery(id+"F2.wireOp",EDGE,"E12.sketch_text.stroke-643"),sQuery(id+"F2.wireOp",EDGE,"E12.sketch_text.stroke-644"),sQuery(id+"F2.wireOp",EDGE,"E12.sketch_text.stroke-645"),sQuery(id+"F2.wireOp",EDGE,"E12.sketch_text.stroke-646"),sQuery(id+"F2.wireOp",EDGE,"E12.sketch_text.stroke-647"),sQuery(id+"F2.wireOp",EDGE,"E12.sketch_text.stroke-648"),sQuery(id+"F2.wireOp",EDGE,"E12.sketch_text.stroke-649"),sQuery(id+"F2.wireOp",EDGE,"E12.sketch_text.stroke-650"),sQuery(id+"F2.wireOp",EDGE,"E12.sketch_text.stroke-651"),sQuery(id+"F2.wireOp",EDGE,"E12.sketch_text.stroke-652"),sQuery(id+"F2.wireOp",EDGE,"E12.sketch_text.stroke-653"),sQuery(id+"F2.wireOp",EDGE,"E12.sketch_text.stroke-654"),sQuery(id+"F2.wireOp",EDGE,"E12.sketch_text.stroke-655"),sQuery(id+"F2.wireOp",EDGE,"E12.sketch_text.stroke-656"),sQuery(id+"F2.wireOp",EDGE,"E12.sketch_text.stroke-657"),sQuery(id+"F2.wireOp",EDGE,"E12.sketch_text.stroke-658"),sQuery(id+"F2.wireOp",EDGE,"E12.sketch_text.stroke-659")])],"isStart":false})});
            var Q14;
            Q14=makeQuery(id+"F3.boolean.opBoolean","COPY",FACE,{"derivedFrom":makeQuery(id+"F3.opExtrude","CAP_FACE",FACE,{"disambiguationData":[OSD([sQuery(id+"F2.wireOp",EDGE,"E22.sketch_text.stroke-0"),sQuery(id+"F2.wireOp",EDGE,"E22.sketch_text.stroke-1"),sQuery(id+"F2.wireOp",EDGE,"E22.sketch_text.stroke-2"),sQuery(id+"F2.wireOp",EDGE,"E22.sketch_text.stroke-3"),sQuery(id+"F2.wireOp",EDGE,"E22.sketch_text.stroke-4"),sQuery(id+"F2.wireOp",EDGE,"E22.sketch_text.stroke-5"),sQuery(id+"F2.wireOp",EDGE,"E22.sketch_text.stroke-6")])],"isStart":false})});
            var Q15;
            Q15=makeQuery(id+"F3.boolean.opBoolean","COPY",FACE,{"derivedFrom":makeQuery(id+"F3.opExtrude","CAP_FACE",FACE,{"disambiguationData":[OSD([sQuery(id+"F2.wireOp",EDGE,"E22.sketch_text.stroke-15"),sQuery(id+"F2.wireOp",EDGE,"E22.sketch_text.stroke-16"),sQuery(id+"F2.wireOp",EDGE,"E22.sketch_text.stroke-17"),sQuery(id+"F2.wireOp",EDGE,"E22.sketch_text.stroke-18"),sQuery(id+"F2.wireOp",EDGE,"E22.sketch_text.stroke-19"),sQuery(id+"F2.wireOp",EDGE,"E22.sketch_text.stroke-20"),sQuery(id+"F2.wireOp",EDGE,"E22.sketch_text.stroke-21"),sQuery(id+"F2.wireOp",EDGE,"E22.sketch_text.stroke-22"),sQuery(id+"F2.wireOp",EDGE,"E22.sketch_text.stroke-23"),sQuery(id+"F2.wireOp",EDGE,"E22.sketch_text.stroke-24"),sQuery(id+"F2.wireOp",EDGE,"E22.sketch_text.stroke-25"),sQuery(id+"F2.wireOp",EDGE,"E22.sketch_text.stroke-26"),sQuery(id+"F2.wireOp",EDGE,"E22.sketch_text.stroke-27"),sQuery(id+"F2.wireOp",EDGE,"E22.sketch_text.stroke-28"),sQuery(id+"F2.wireOp",EDGE,"E22.sketch_text.stroke-29"),sQuery(id+"F2.wireOp",EDGE,"E22.sketch_text.stroke-30"),sQuery(id+"F2.wireOp",EDGE,"E22.sketch_text.stroke-31"),sQuery(id+"F2.wireOp",EDGE,"E22.sketch_text.stroke-32"),sQuery(id+"F2.wireOp",EDGE,"E22.sketch_text.stroke-33"),sQuery(id+"F2.wireOp",EDGE,"E22.sketch_text.stroke-34"),sQuery(id+"F2.wireOp",EDGE,"E22.sketch_text.stroke-35")])],"isStart":false})});
            var Q16;
            Q16=makeQuery(id+"F3.boolean.opBoolean","COPY",FACE,{"derivedFrom":makeQuery(id+"F3.opExtrude","CAP_FACE",FACE,{"disambiguationData":[OSD([sQuery(id+"F2.wireOp",EDGE,"E22.sketch_text.stroke-7"),sQuery(id+"F2.wireOp",EDGE,"E22.sketch_text.stroke-8"),sQuery(id+"F2.wireOp",EDGE,"E22.sketch_text.stroke-9"),sQuery(id+"F2.wireOp",EDGE,"E22.sketch_text.stroke-10"),sQuery(id+"F2.wireOp",EDGE,"E22.sketch_text.stroke-11"),sQuery(id+"F2.wireOp",EDGE,"E22.sketch_text.stroke-12"),sQuery(id+"F2.wireOp",EDGE,"E22.sketch_text.stroke-13"),sQuery(id+"F2.wireOp",EDGE,"E22.sketch_text.stroke-14")])],"isStart":false})});
            var Q17;
            Q17=makeQuery(id+"F3.boolean.opBoolean","COPY",FACE,{"derivedFrom":makeQuery(id+"F3.opExtrude","CAP_FACE",FACE,{"disambiguationData":[OSD([sQuery(id+"F2.wireOp",EDGE,"E22.sketch_text.stroke-36"),sQuery(id+"F2.wireOp",EDGE,"E22.sketch_text.stroke-37"),sQuery(id+"F2.wireOp",EDGE,"E22.sketch_text.stroke-38"),sQuery(id+"F2.wireOp",EDGE,"E22.sketch_text.stroke-39"),sQuery(id+"F2.wireOp",EDGE,"E22.sketch_text.stroke-40"),sQuery(id+"F2.wireOp",EDGE,"E22.sketch_text.stroke-41"),sQuery(id+"F2.wireOp",EDGE,"E22.sketch_text.stroke-42"),sQuery(id+"F2.wireOp",EDGE,"E22.sketch_text.stroke-43")])],"isStart":false})});
            var Q18;
            Q18=makeQuery(id+"F3.boolean.opBoolean","COPY",FACE,{"derivedFrom":makeQuery(id+"F3.opExtrude","CAP_FACE",FACE,{"disambiguationData":[OSD([sQuery(id+"F2.wireOp",EDGE,"E22.sketch_text.stroke-44"),sQuery(id+"F2.wireOp",EDGE,"E22.sketch_text.stroke-45"),sQuery(id+"F2.wireOp",EDGE,"E22.sketch_text.stroke-46"),sQuery(id+"F2.wireOp",EDGE,"E22.sketch_text.stroke-47"),sQuery(id+"F2.wireOp",EDGE,"E22.sketch_text.stroke-48"),sQuery(id+"F2.wireOp",EDGE,"E22.sketch_text.stroke-49"),sQuery(id+"F2.wireOp",EDGE,"E22.sketch_text.stroke-50"),sQuery(id+"F2.wireOp",EDGE,"E22.sketch_text.stroke-51"),sQuery(id+"F2.wireOp",EDGE,"E22.sketch_text.stroke-52"),sQuery(id+"F2.wireOp",EDGE,"E22.sketch_text.stroke-53"),sQuery(id+"F2.wireOp",EDGE,"E22.sketch_text.stroke-54"),sQuery(id+"F2.wireOp",EDGE,"E22.sketch_text.stroke-55"),sQuery(id+"F2.wireOp",EDGE,"E22.sketch_text.stroke-56"),sQuery(id+"F2.wireOp",EDGE,"E22.sketch_text.stroke-57"),sQuery(id+"F2.wireOp",EDGE,"E22.sketch_text.stroke-58"),sQuery(id+"F2.wireOp",EDGE,"E22.sketch_text.stroke-59"),sQuery(id+"F2.wireOp",EDGE,"E22.sketch_text.stroke-60"),sQuery(id+"F2.wireOp",EDGE,"E22.sketch_text.stroke-61"),sQuery(id+"F2.wireOp",EDGE,"E22.sketch_text.stroke-62"),sQuery(id+"F2.wireOp",EDGE,"E22.sketch_text.stroke-63"),sQuery(id+"F2.wireOp",EDGE,"E22.sketch_text.stroke-64"),sQuery(id+"F2.wireOp",EDGE,"E22.sketch_text.stroke-65"),sQuery(id+"F2.wireOp",EDGE,"E22.sketch_text.stroke-66"),sQuery(id+"F2.wireOp",EDGE,"E22.sketch_text.stroke-67"),sQuery(id+"F2.wireOp",EDGE,"E22.sketch_text.stroke-68"),sQuery(id+"F2.wireOp",EDGE,"E22.sketch_text.stroke-69"),sQuery(id+"F2.wireOp",EDGE,"E22.sketch_text.stroke-70"),sQuery(id+"F2.wireOp",EDGE,"E22.sketch_text.stroke-71"),sQuery(id+"F2.wireOp",EDGE,"E22.sketch_text.stroke-72"),sQuery(id+"F2.wireOp",EDGE,"E22.sketch_text.stroke-73"),sQuery(id+"F2.wireOp",EDGE,"E22.sketch_text.stroke-74"),sQuery(id+"F2.wireOp",EDGE,"E22.sketch_text.stroke-75"),sQuery(id+"F2.wireOp",EDGE,"E22.sketch_text.stroke-76")])],"isStart":false})});
            var Q19;
            Q19=makeQuery(id+"F3.boolean.opBoolean","COPY",FACE,{"derivedFrom":makeQuery(id+"F3.opExtrude","CAP_FACE",FACE,{"disambiguationData":[OSD([sQuery(id+"F2.wireOp",EDGE,"E22.sketch_text.stroke-77"),sQuery(id+"F2.wireOp",EDGE,"E22.sketch_text.stroke-78"),sQuery(id+"F2.wireOp",EDGE,"E22.sketch_text.stroke-79"),sQuery(id+"F2.wireOp",EDGE,"E22.sketch_text.stroke-80"),sQuery(id+"F2.wireOp",EDGE,"E22.sketch_text.stroke-81"),sQuery(id+"F2.wireOp",EDGE,"E22.sketch_text.stroke-82"),sQuery(id+"F2.wireOp",EDGE,"E22.sketch_text.stroke-83"),sQuery(id+"F2.wireOp",EDGE,"E22.sketch_text.stroke-84"),sQuery(id+"F2.wireOp",EDGE,"E22.sketch_text.stroke-85"),sQuery(id+"F2.wireOp",EDGE,"E22.sketch_text.stroke-86"),sQuery(id+"F2.wireOp",EDGE,"E22.sketch_text.stroke-87"),sQuery(id+"F2.wireOp",EDGE,"E22.sketch_text.stroke-88"),sQuery(id+"F2.wireOp",EDGE,"E22.sketch_text.stroke-89"),sQuery(id+"F2.wireOp",EDGE,"E22.sketch_text.stroke-90"),sQuery(id+"F2.wireOp",EDGE,"E22.sketch_text.stroke-91"),sQuery(id+"F2.wireOp",EDGE,"E22.sketch_text.stroke-92"),sQuery(id+"F2.wireOp",EDGE,"E22.sketch_text.stroke-93"),sQuery(id+"F2.wireOp",EDGE,"E22.sketch_text.stroke-94"),sQuery(id+"F2.wireOp",EDGE,"E22.sketch_text.stroke-95"),sQuery(id+"F2.wireOp",EDGE,"E22.sketch_text.stroke-96"),sQuery(id+"F2.wireOp",EDGE,"E22.sketch_text.stroke-97")])],"isStart":false})});
            var Q20;
            Q20=makeQuery(id+"F3.boolean.opBoolean","COPY",FACE,{"derivedFrom":makeQuery(id+"F3.opExtrude","CAP_FACE",FACE,{"disambiguationData":[OSD([sQuery(id+"F2.wireOp",EDGE,"E22.sketch_text.stroke-98"),sQuery(id+"F2.wireOp",EDGE,"E22.sketch_text.stroke-99"),sQuery(id+"F2.wireOp",EDGE,"E22.sketch_text.stroke-100"),sQuery(id+"F2.wireOp",EDGE,"E22.sketch_text.stroke-101"),sQuery(id+"F2.wireOp",EDGE,"E22.sketch_text.stroke-102"),sQuery(id+"F2.wireOp",EDGE,"E22.sketch_text.stroke-103"),sQuery(id+"F2.wireOp",EDGE,"E22.sketch_text.stroke-104"),sQuery(id+"F2.wireOp",EDGE,"E22.sketch_text.stroke-105"),sQuery(id+"F2.wireOp",EDGE,"E22.sketch_text.stroke-106"),sQuery(id+"F2.wireOp",EDGE,"E22.sketch_text.stroke-107"),sQuery(id+"F2.wireOp",EDGE,"E22.sketch_text.stroke-108"),sQuery(id+"F2.wireOp",EDGE,"E22.sketch_text.stroke-109"),sQuery(id+"F2.wireOp",EDGE,"E22.sketch_text.stroke-110"),sQuery(id+"F2.wireOp",EDGE,"E22.sketch_text.stroke-111"),sQuery(id+"F2.wireOp",EDGE,"E22.sketch_text.stroke-112"),sQuery(id+"F2.wireOp",EDGE,"E22.sketch_text.stroke-113"),sQuery(id+"F2.wireOp",EDGE,"E22.sketch_text.stroke-114"),sQuery(id+"F2.wireOp",EDGE,"E22.sketch_text.stroke-115"),sQuery(id+"F2.wireOp",EDGE,"E22.sketch_text.stroke-116"),sQuery(id+"F2.wireOp",EDGE,"E22.sketch_text.stroke-117"),sQuery(id+"F2.wireOp",EDGE,"E22.sketch_text.stroke-118"),sQuery(id+"F2.wireOp",EDGE,"E22.sketch_text.stroke-119"),sQuery(id+"F2.wireOp",EDGE,"E22.sketch_text.stroke-120"),sQuery(id+"F2.wireOp",EDGE,"E22.sketch_text.stroke-121"),sQuery(id+"F2.wireOp",EDGE,"E22.sketch_text.stroke-122"),sQuery(id+"F2.wireOp",EDGE,"E22.sketch_text.stroke-123"),sQuery(id+"F2.wireOp",EDGE,"E22.sketch_text.stroke-124"),sQuery(id+"F2.wireOp",EDGE,"E22.sketch_text.stroke-125")])],"isStart":false})});
            var Q21;
            Q21=makeQuery(id+"F3.boolean.opBoolean","COPY",FACE,{"derivedFrom":makeQuery(id+"F3.opExtrude","CAP_FACE",FACE,{"disambiguationData":[OSD([sQuery(id+"F2.wireOp",EDGE,"E22.sketch_text.stroke-134"),sQuery(id+"F2.wireOp",EDGE,"E22.sketch_text.stroke-135"),sQuery(id+"F2.wireOp",EDGE,"E22.sketch_text.stroke-136"),sQuery(id+"F2.wireOp",EDGE,"E22.sketch_text.stroke-137"),sQuery(id+"F2.wireOp",EDGE,"E22.sketch_text.stroke-138"),sQuery(id+"F2.wireOp",EDGE,"E22.sketch_text.stroke-139"),sQuery(id+"F2.wireOp",EDGE,"E22.sketch_text.stroke-140")])],"isStart":false})});
            var Q22;
            Q22=makeQuery(id+"F3.boolean.opBoolean","COPY",FACE,{"derivedFrom":makeQuery(id+"F3.opExtrude","CAP_FACE",FACE,{"disambiguationData":[OSD([sQuery(id+"F2.wireOp",EDGE,"E22.sketch_text.stroke-149"),sQuery(id+"F2.wireOp",EDGE,"E22.sketch_text.stroke-150"),sQuery(id+"F2.wireOp",EDGE,"E22.sketch_text.stroke-151"),sQuery(id+"F2.wireOp",EDGE,"E22.sketch_text.stroke-152"),sQuery(id+"F2.wireOp",EDGE,"E22.sketch_text.stroke-153"),sQuery(id+"F2.wireOp",EDGE,"E22.sketch_text.stroke-154"),sQuery(id+"F2.wireOp",EDGE,"E22.sketch_text.stroke-155"),sQuery(id+"F2.wireOp",EDGE,"E22.sketch_text.stroke-156"),sQuery(id+"F2.wireOp",EDGE,"E22.sketch_text.stroke-157"),sQuery(id+"F2.wireOp",EDGE,"E22.sketch_text.stroke-158"),sQuery(id+"F2.wireOp",EDGE,"E22.sketch_text.stroke-159"),sQuery(id+"F2.wireOp",EDGE,"E22.sketch_text.stroke-160"),sQuery(id+"F2.wireOp",EDGE,"E22.sketch_text.stroke-161"),sQuery(id+"F2.wireOp",EDGE,"E22.sketch_text.stroke-162"),sQuery(id+"F2.wireOp",EDGE,"E22.sketch_text.stroke-163"),sQuery(id+"F2.wireOp",EDGE,"E22.sketch_text.stroke-164"),sQuery(id+"F2.wireOp",EDGE,"E22.sketch_text.stroke-165"),sQuery(id+"F2.wireOp",EDGE,"E22.sketch_text.stroke-166"),sQuery(id+"F2.wireOp",EDGE,"E22.sketch_text.stroke-167"),sQuery(id+"F2.wireOp",EDGE,"E22.sketch_text.stroke-168"),sQuery(id+"F2.wireOp",EDGE,"E22.sketch_text.stroke-169")])],"isStart":false})});
            var Q23;
            Q23=makeQuery(id+"F3.boolean.opBoolean","COPY",FACE,{"derivedFrom":makeQuery(id+"F3.opExtrude","CAP_FACE",FACE,{"disambiguationData":[OSD([sQuery(id+"F2.wireOp",EDGE,"E22.sketch_text.stroke-170"),sQuery(id+"F2.wireOp",EDGE,"E22.sketch_text.stroke-171"),sQuery(id+"F2.wireOp",EDGE,"E22.sketch_text.stroke-172"),sQuery(id+"F2.wireOp",EDGE,"E22.sketch_text.stroke-173"),sQuery(id+"F2.wireOp",EDGE,"E22.sketch_text.stroke-174"),sQuery(id+"F2.wireOp",EDGE,"E22.sketch_text.stroke-175"),sQuery(id+"F2.wireOp",EDGE,"E22.sketch_text.stroke-176"),sQuery(id+"F2.wireOp",EDGE,"E22.sketch_text.stroke-177"),sQuery(id+"F2.wireOp",EDGE,"E22.sketch_text.stroke-178"),sQuery(id+"F2.wireOp",EDGE,"E22.sketch_text.stroke-179"),sQuery(id+"F2.wireOp",EDGE,"E22.sketch_text.stroke-180"),sQuery(id+"F2.wireOp",EDGE,"E22.sketch_text.stroke-181"),sQuery(id+"F2.wireOp",EDGE,"E22.sketch_text.stroke-182"),sQuery(id+"F2.wireOp",EDGE,"E22.sketch_text.stroke-183"),sQuery(id+"F2.wireOp",EDGE,"E22.sketch_text.stroke-184"),sQuery(id+"F2.wireOp",EDGE,"E22.sketch_text.stroke-185"),sQuery(id+"F2.wireOp",EDGE,"E22.sketch_text.stroke-186"),sQuery(id+"F2.wireOp",EDGE,"E22.sketch_text.stroke-187")])],"isStart":false})});
            var Q24;
            Q24=makeQuery(id+"F3.boolean.opBoolean","COPY",FACE,{"derivedFrom":makeQuery(id+"F3.opExtrude","CAP_FACE",FACE,{"disambiguationData":[OSD([sQuery(id+"F2.wireOp",EDGE,"E22.sketch_text.stroke-188"),sQuery(id+"F2.wireOp",EDGE,"E22.sketch_text.stroke-189"),sQuery(id+"F2.wireOp",EDGE,"E22.sketch_text.stroke-190"),sQuery(id+"F2.wireOp",EDGE,"E22.sketch_text.stroke-191"),sQuery(id+"F2.wireOp",EDGE,"E22.sketch_text.stroke-192"),sQuery(id+"F2.wireOp",EDGE,"E22.sketch_text.stroke-193"),sQuery(id+"F2.wireOp",EDGE,"E22.sketch_text.stroke-194"),sQuery(id+"F2.wireOp",EDGE,"E22.sketch_text.stroke-195"),sQuery(id+"F2.wireOp",EDGE,"E22.sketch_text.stroke-196")])],"isStart":false})});
            var Q25;
            Q25=makeQuery(id+"F3.boolean.opBoolean","COPY",FACE,{"derivedFrom":makeQuery(id+"F3.opExtrude","CAP_FACE",FACE,{"disambiguationData":[OSD([sQuery(id+"F2.wireOp",EDGE,"E22.sketch_text.stroke-197"),sQuery(id+"F2.wireOp",EDGE,"E22.sketch_text.stroke-198"),sQuery(id+"F2.wireOp",EDGE,"E22.sketch_text.stroke-199"),sQuery(id+"F2.wireOp",EDGE,"E22.sketch_text.stroke-200"),sQuery(id+"F2.wireOp",EDGE,"E22.sketch_text.stroke-201"),sQuery(id+"F2.wireOp",EDGE,"E22.sketch_text.stroke-202"),sQuery(id+"F2.wireOp",EDGE,"E22.sketch_text.stroke-203"),sQuery(id+"F2.wireOp",EDGE,"E22.sketch_text.stroke-204"),sQuery(id+"F2.wireOp",EDGE,"E22.sketch_text.stroke-205"),sQuery(id+"F2.wireOp",EDGE,"E22.sketch_text.stroke-206"),sQuery(id+"F2.wireOp",EDGE,"E22.sketch_text.stroke-207"),sQuery(id+"F2.wireOp",EDGE,"E22.sketch_text.stroke-208"),sQuery(id+"F2.wireOp",EDGE,"E22.sketch_text.stroke-209"),sQuery(id+"F2.wireOp",EDGE,"E22.sketch_text.stroke-210"),sQuery(id+"F2.wireOp",EDGE,"E22.sketch_text.stroke-211"),sQuery(id+"F2.wireOp",EDGE,"E22.sketch_text.stroke-212"),sQuery(id+"F2.wireOp",EDGE,"E22.sketch_text.stroke-213"),sQuery(id+"F2.wireOp",EDGE,"E22.sketch_text.stroke-214"),sQuery(id+"F2.wireOp",EDGE,"E22.sketch_text.stroke-215"),sQuery(id+"F2.wireOp",EDGE,"E22.sketch_text.stroke-216"),sQuery(id+"F2.wireOp",EDGE,"E22.sketch_text.stroke-217"),sQuery(id+"F2.wireOp",EDGE,"E22.sketch_text.stroke-218"),sQuery(id+"F2.wireOp",EDGE,"E22.sketch_text.stroke-219"),sQuery(id+"F2.wireOp",EDGE,"E22.sketch_text.stroke-220"),sQuery(id+"F2.wireOp",EDGE,"E22.sketch_text.stroke-221"),sQuery(id+"F2.wireOp",EDGE,"E22.sketch_text.stroke-222"),sQuery(id+"F2.wireOp",EDGE,"E22.sketch_text.stroke-223")])],"isStart":false})});
            var Q26;
            Q26=makeQuery(id+"F3.boolean.opBoolean","COPY",FACE,{"derivedFrom":makeQuery(id+"F3.opExtrude","CAP_FACE",FACE,{"disambiguationData":[OSD([sQuery(id+"F2.wireOp",EDGE,"E12.sketch_text.stroke-244"),sQuery(id+"F2.wireOp",EDGE,"E12.sketch_text.stroke-245"),sQuery(id+"F2.wireOp",EDGE,"E12.sketch_text.stroke-246"),sQuery(id+"F2.wireOp",EDGE,"E12.sketch_text.stroke-247"),sQuery(id+"F2.wireOp",EDGE,"E12.sketch_text.stroke-248"),sQuery(id+"F2.wireOp",EDGE,"E12.sketch_text.stroke-249"),sQuery(id+"F2.wireOp",EDGE,"E12.sketch_text.stroke-250"),sQuery(id+"F2.wireOp",EDGE,"E12.sketch_text.stroke-251"),sQuery(id+"F2.wireOp",EDGE,"E12.sketch_text.stroke-252"),sQuery(id+"F2.wireOp",EDGE,"E12.sketch_text.stroke-253"),sQuery(id+"F2.wireOp",EDGE,"E12.sketch_text.stroke-254"),sQuery(id+"F2.wireOp",EDGE,"E12.sketch_text.stroke-255"),sQuery(id+"F2.wireOp",EDGE,"E12.sketch_text.stroke-256"),sQuery(id+"F2.wireOp",EDGE,"E12.sketch_text.stroke-257"),sQuery(id+"F2.wireOp",EDGE,"E12.sketch_text.stroke-258"),sQuery(id+"F2.wireOp",EDGE,"E12.sketch_text.stroke-259")])],"isStart":false})});
            extrude(context, id + "F7", {"entities" : qUnion([Q0, Q1, Q2, Q3, Q4, Q5, Q6, Q7, Q8, Q9, Q10, Q11, Q12, Q13, Q14, Q15, Q16, Q17, Q18, Q19, Q20, Q21, Q22, Q23, Q24, Q25, Q26]), "depth" : 5 * mm});
        }
        {
            var Q0;
            Q0=makeQuery(id+"F3.boolean.opBoolean","COPY",FACE,{"derivedFrom":makeQuery(id+"F3.opExtrude","CAP_FACE",FACE,{"disambiguationData":[OSD([sQuery(id+"F2.wireOp",EDGE,"E22.sketch_text.stroke-126"),sQuery(id+"F2.wireOp",EDGE,"E22.sketch_text.stroke-127"),sQuery(id+"F2.wireOp",EDGE,"E22.sketch_text.stroke-128"),sQuery(id+"F2.wireOp",EDGE,"E22.sketch_text.stroke-129"),sQuery(id+"F2.wireOp",EDGE,"E22.sketch_text.stroke-130"),sQuery(id+"F2.wireOp",EDGE,"E22.sketch_text.stroke-131"),sQuery(id+"F2.wireOp",EDGE,"E22.sketch_text.stroke-132"),sQuery(id+"F2.wireOp",EDGE,"E22.sketch_text.stroke-133")])],"isStart":false})});
            var Q1;
            Q1=makeQuery(id+"F3.boolean.opBoolean","COPY",FACE,{"derivedFrom":makeQuery(id+"F3.opExtrude","CAP_FACE",FACE,{"disambiguationData":[OSD([sQuery(id+"F2.wireOp",EDGE,"E22.sketch_text.stroke-141"),sQuery(id+"F2.wireOp",EDGE,"E22.sketch_text.stroke-142"),sQuery(id+"F2.wireOp",EDGE,"E22.sketch_text.stroke-143"),sQuery(id+"F2.wireOp",EDGE,"E22.sketch_text.stroke-144"),sQuery(id+"F2.wireOp",EDGE,"E22.sketch_text.stroke-145"),sQuery(id+"F2.wireOp",EDGE,"E22.sketch_text.stroke-146"),sQuery(id+"F2.wireOp",EDGE,"E22.sketch_text.stroke-147"),sQuery(id+"F2.wireOp",EDGE,"E22.sketch_text.stroke-148")])],"isStart":false})});
            extrude(context, id + "F8", {"entities" : qUnion([Q0, Q1]), "depth" : 5 * mm});
        }
        {
            var Q0;
            Q0=makeQuery(id+"F3.boolean.opBoolean","COPY",FACE,{"derivedFrom":makeQuery(id+"F3.opExtrude","CAP_FACE",FACE,{"disambiguationData":[OSD([sQuery(id+"F2.wireOp",EDGE,"E17"),sQuery(id+"F2.wireOp",EDGE,"E18"),sQuery(id+"F2.wireOp",EDGE,"E19"),sQuery(id+"F2.wireOp",EDGE,"E20")])],"isStart":false})});
            extrude(context, id + "F9", {"entities" : qUnion([Q0]), "depth" : 5 * mm});
        }
    });
